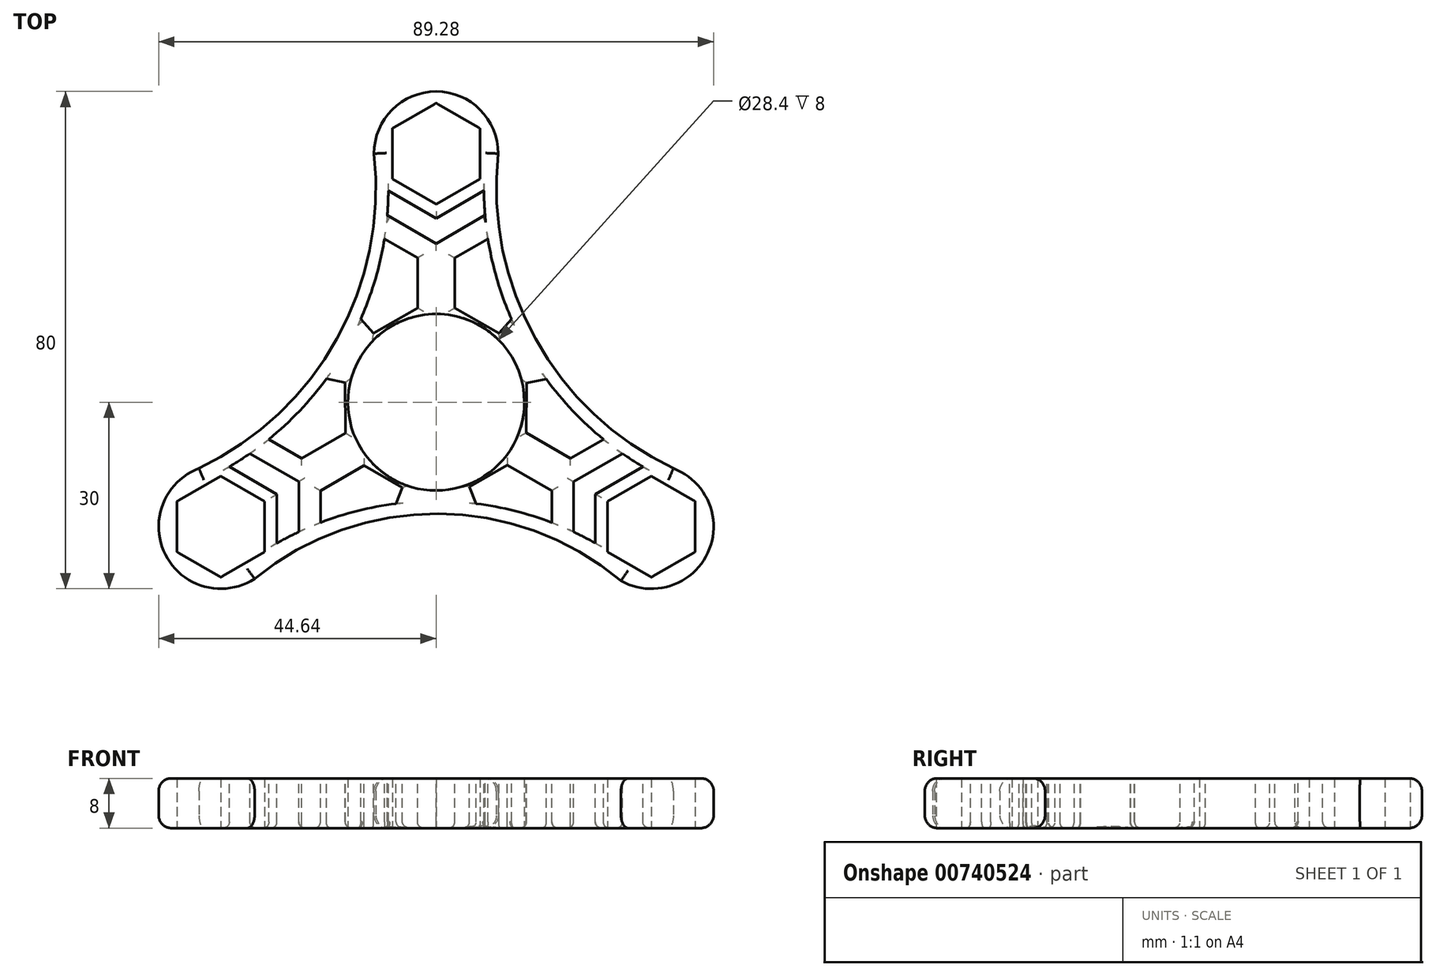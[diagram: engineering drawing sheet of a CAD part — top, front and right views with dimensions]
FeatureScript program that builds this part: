
annotation { "Feature Type Name" : "Feature", "Feature Type Description" : "" }
export const myFeature = defineFeature(function(context is Context, id is Id, definition is map)
    precondition{}
    {
        {
            var Q0;
            Q0=qCreatedBy(makeId("Top.planeOp"),FACE);
            var sketch = newSketch(context, id + "F0", { "sketchPlane" : qUnion([Q0])});
            skPoint(sketch, "E0.0.midPoint", {"position": v(0, 13.42) * mm});
            skLineSegment(sketch, "E1", {"start": v(0, 0) * mm, "end": v(0, 40) * mm});
            skLineSegment(sketch, "E2", {"start": v(0, 0) * mm, "end": v(-34.64, -20) * mm});
            skLineSegment(sketch, "E3", {"start": v(0, 0) * mm, "end": v(34.64, -20) * mm});
            skCircle(sketch, "E4.cCircle", {"center": v(0, 40) * mm, "radius": 7.05 * mm, "construction": true});
            skLineSegment(sketch, "E4.0", {"start": v(-7.05, 35.93) * mm, "end": v(-7.05, 44.07) * mm});
            skLineSegment(sketch, "E4.1", {"start": v(-7.05, 44.07) * mm, "end": v(0, 48.14) * mm});
            skLineSegment(sketch, "E4.2", {"start": v(0, 48.14) * mm, "end": v(7.05, 44.07) * mm});
            skLineSegment(sketch, "E4.3", {"start": v(7.05, 44.07) * mm, "end": v(7.05, 35.93) * mm});
            skLineSegment(sketch, "E4.4", {"start": v(7.05, 35.93) * mm, "end": v(0, 31.86) * mm});
            skLineSegment(sketch, "E4.5", {"start": v(0, 31.86) * mm, "end": v(-7.05, 35.93) * mm});
            skPoint(sketch, "E4.0.midPoint", {"position": v(-7.05, 40) * mm});
            skCircle(sketch, "E5.cCircle", {"center": v(-34.64, -20) * mm, "radius": 7.05 * mm, "construction": true});
            skLineSegment(sketch, "E5.0", {"start": v(-41.7, -24.07) * mm, "end": v(-41.7, -15.93) * mm});
            skLineSegment(sketch, "E5.1", {"start": v(-41.7, -15.93) * mm, "end": v(-34.64, -11.86) * mm});
            skLineSegment(sketch, "E5.2", {"start": v(-34.64, -11.86) * mm, "end": v(-27.6, -15.93) * mm});
            skLineSegment(sketch, "E5.3", {"start": v(-27.6, -15.93) * mm, "end": v(-27.6, -24.07) * mm});
            skLineSegment(sketch, "E5.4", {"start": v(-27.6, -24.07) * mm, "end": v(-34.64, -28.14) * mm});
            skLineSegment(sketch, "E5.5", {"start": v(-34.64, -28.14) * mm, "end": v(-41.7, -24.07) * mm});
            skPoint(sketch, "E5.0.midPoint", {"position": v(-41.7, -20) * mm});
            skCircle(sketch, "E6.cCircle", {"center": v(34.64, -20) * mm, "radius": 7.05 * mm, "construction": true});
            skLineSegment(sketch, "E6.0", {"start": v(41.7, -15.93) * mm, "end": v(41.7, -24.07) * mm});
            skLineSegment(sketch, "E6.1", {"start": v(41.7, -24.07) * mm, "end": v(34.64, -28.14) * mm});
            skLineSegment(sketch, "E6.2", {"start": v(34.64, -28.14) * mm, "end": v(27.6, -24.07) * mm});
            skLineSegment(sketch, "E6.3", {"start": v(27.6, -24.07) * mm, "end": v(27.6, -15.93) * mm});
            skLineSegment(sketch, "E6.4", {"start": v(27.6, -15.93) * mm, "end": v(34.64, -11.86) * mm});
            skLineSegment(sketch, "E6.5", {"start": v(34.64, -11.86) * mm, "end": v(41.7, -15.93) * mm});
            skPoint(sketch, "E6.0.midPoint", {"position": v(41.7, -20) * mm});
            skCircle(sketch, "E7", {"center": v(0, 40) * mm, "radius": 10 * mm});
            skCircle(sketch, "E8", {"center": v(-34.64, -20) * mm, "radius": 10 * mm});
            skCircle(sketch, "E9", {"center": v(34.64, -20) * mm, "radius": 10 * mm});
            skArc(sketch, "E10", {"start": v(-38.17, -10.64) * mm, "mid": v(-16, 10.18) * mm, "end": v(-10, 40) * mm});
            skPoint(sketch, "E10.startSnap0", {"position": v(-38.17, -13.9) * mm});
            skPoint(sketch, "E11.startSnap0", {"position": v(31.12, -26.1) * mm});
            skPoint(sketch, "E11.endSnap0", {"position": v(-31.12, -26.1) * mm});
            skArc(sketch, "E12", {"start": v(10, 40) * mm, "mid": v(16, 10.18) * mm, "end": v(38.17, -10.64) * mm});
            skPoint(sketch, "E12.startSnap0", {"position": v(7.05, 40) * mm});
            skPoint(sketch, "E12.endSnap0", {"position": v(38.17, -13.9) * mm});
            skCircle(sketch, "E13", {"center": v(0, 0) * mm, "radius": 14.2 * mm});
            skArc(sketch, "E14", {"start": v(29.75, -28.72) * mm, "mid": v(0.32, -17.94) * mm, "end": v(-29.22, -28.4) * mm});
            skSolve(sketch);
        }
        {
            var Q0;
            {var subQ0=sQuery(id+"F0.wireOp",EDGE,"E10");var subQ1=sQuery(id+"F0.wireOp",EDGE,"E0.0");var subQ2=makeQuery(id+"F0.imprint","INTERSECT",VERTEX,{"derivedFrom":[subQ1,subQ0]});Q0=makeQuery(id+"F0.imprint","IMPRINT",FACE,{"disambiguationData":[TD([[makeQuery(id+"F0.imprint","IMPRINT",EDGE,{"disambiguationData":[TD([[subQ2,-1.0]])],"derivedFrom":subQ1}),1.0]])]});}
            var Q1;
            Q1=makeQuery(id+"F0.imprint","IMPRINT",FACE,{"disambiguationData":[TD([[makeQuery(id+"F0.imprint","IMPRINT",EDGE,{"derivedFrom":sQuery(id+"F0.wireOp",EDGE,"E4.0")}),1.0]])]});
            var Q2;
            {var subQ0=sQuery(id+"F0.wireOp",EDGE,"E12");var subQ1=sQuery(id+"F0.wireOp",EDGE,"E0.0");var subQ2=makeQuery(id+"F0.imprint","INTERSECT",VERTEX,{"derivedFrom":[subQ1,subQ0]});Q2=makeQuery(id+"F0.imprint","IMPRINT",FACE,{"disambiguationData":[TD([[makeQuery(id+"F0.imprint","IMPRINT",EDGE,{"disambiguationData":[TD([[subQ2,1.0]])],"derivedFrom":subQ1}),1.0]])]});}
            var Q3;
            {var subQ1=sQuery(id+"F0.wireOp",EDGE,"vRD934ja-ZAdI-i6bS-saWl-KqptXDvDajmV");var subQ8=sQuery(id+"F0.wireOp",EDGE,"E2");var subQ11=makeQuery(id+"F0.imprint","INTERSECT",VERTEX,{"derivedFrom":[subQ1,subQ8]});Q3=makeQuery(id+"F0.imprint","IMPRINT",FACE,{"disambiguationData":[TD([[makeQuery(id+"F0.imprint","IMPRINT",EDGE,{"disambiguationData":[TD([[subQ11,1.0]])],"derivedFrom":subQ1}),-1.0]])]});}
            var Q4;
            {var subQ0=sQuery(id+"F0.wireOp",EDGE,"E1");var subQ1=sQuery(id+"F0.wireOp",EDGE,"vRD934ja-ZAdI-i6bS-saWl-KqptXDvDajmV");var subQ2=makeQuery(id+"F0.imprint","INTERSECT",VERTEX,{"derivedFrom":[subQ1,subQ0]});Q4=makeQuery(id+"F0.imprint","IMPRINT",FACE,{"disambiguationData":[TD([[makeQuery(id+"F0.imprint","IMPRINT",EDGE,{"disambiguationData":[TD([[subQ2,1.0]])],"derivedFrom":subQ1}),-1.0]])]});}
            var Q5;
            {var subQ3=sQuery(id+"F0.wireOp",EDGE,"E2");var subQ5=sQuery(id+"F0.wireOp",EDGE,"vRD934ja-ZAdI-i6bS-saWl-KqptXDvDajmV");var subQ6=makeQuery(id+"F0.imprint","INTERSECT",VERTEX,{"derivedFrom":[subQ5,subQ3]});Q5=makeQuery(id+"F0.imprint","IMPRINT",FACE,{"disambiguationData":[TD([[makeQuery(id+"F0.imprint","IMPRINT",EDGE,{"disambiguationData":[TD([[subQ6,-1.0]])],"derivedFrom":subQ5}),-1.0]])]});}
            var Q6;
            {var subQ0=sQuery(id+"F0.wireOp",EDGE,"E11");var subQ1=sQuery(id+"F0.wireOp",EDGE,"E0.2");var subQ2=makeQuery(id+"F0.imprint","INTERSECT",VERTEX,{"derivedFrom":[subQ1,subQ0]});Q6=makeQuery(id+"F0.imprint","IMPRINT",FACE,{"disambiguationData":[TD([[makeQuery(id+"F0.imprint","IMPRINT",EDGE,{"disambiguationData":[TD([[subQ2,-1.0]])],"derivedFrom":subQ1}),1.0]])]});}
            var Q7;
            {var subQ0=sQuery(id+"F0.wireOp",EDGE,"E10");var subQ1=sQuery(id+"F0.wireOp",EDGE,"E0.2");var subQ2=makeQuery(id+"F0.imprint","INTERSECT",VERTEX,{"derivedFrom":[subQ1,subQ0]});Q7=makeQuery(id+"F0.imprint","IMPRINT",FACE,{"disambiguationData":[TD([[makeQuery(id+"F0.imprint","IMPRINT",EDGE,{"disambiguationData":[TD([[subQ2,1.0]])],"derivedFrom":subQ1}),1.0]])]});}
            var Q8;
            Q8=makeQuery(id+"F0.imprint","IMPRINT",FACE,{"disambiguationData":[TD([[makeQuery(id+"F0.imprint","IMPRINT",EDGE,{"derivedFrom":sQuery(id+"F0.wireOp",EDGE,"E5.0")}),1.0]])]});
            var Q9;
            {var subQ0=sQuery(id+"F0.wireOp",EDGE,"E11");var subQ1=sQuery(id+"F0.wireOp",EDGE,"E0.1");var subQ2=makeQuery(id+"F0.imprint","INTERSECT",VERTEX,{"derivedFrom":[subQ1,subQ0]});Q9=makeQuery(id+"F0.imprint","IMPRINT",FACE,{"disambiguationData":[TD([[makeQuery(id+"F0.imprint","IMPRINT",EDGE,{"disambiguationData":[TD([[subQ2,1.0]])],"derivedFrom":subQ1}),1.0]])]});}
            var Q10;
            {var subQ0=sQuery(id+"F0.wireOp",EDGE,"E12");var subQ1=sQuery(id+"F0.wireOp",EDGE,"E0.1");var subQ2=makeQuery(id+"F0.imprint","INTERSECT",VERTEX,{"derivedFrom":[subQ1,subQ0]});Q10=makeQuery(id+"F0.imprint","IMPRINT",FACE,{"disambiguationData":[TD([[makeQuery(id+"F0.imprint","IMPRINT",EDGE,{"disambiguationData":[TD([[subQ2,-1.0]])],"derivedFrom":subQ1}),1.0]])]});}
            var Q11;
            Q11=makeQuery(id+"F0.imprint","IMPRINT",FACE,{"disambiguationData":[TD([[makeQuery(id+"F0.imprint","IMPRINT",EDGE,{"derivedFrom":sQuery(id+"F0.wireOp",EDGE,"E6.0")}),1.0]])]});
            var Q12;
            {var subQ6=sQuery(id+"F0.wireOp",EDGE,"E1");var subQ9=sQuery(id+"F0.wireOp",EDGE,"E7");var subQ10=makeQuery(id+"F0.imprint","INTERSECT",VERTEX,{"derivedFrom":[subQ6,subQ9]});Q12=makeQuery(id+"F0.imprint","IMPRINT",FACE,{"disambiguationData":[TD([[makeQuery(id+"F0.imprint","IMPRINT",EDGE,{"disambiguationData":[TD([[subQ10,1.0]])],"derivedFrom":subQ6}),1.0]])]});}
            var Q13;
            {var subQ5=sQuery(id+"F0.wireOp",EDGE,"E7");var subQ6=sQuery(id+"F0.wireOp",EDGE,"E1");var subQ7=makeQuery(id+"F0.imprint","INTERSECT",VERTEX,{"derivedFrom":[subQ6,subQ5]});Q13=makeQuery(id+"F0.imprint","IMPRINT",FACE,{"disambiguationData":[TD([[makeQuery(id+"F0.imprint","IMPRINT",EDGE,{"disambiguationData":[TD([[subQ7,1.0]])],"derivedFrom":subQ6}),-1.0]])]});}
            var Q14;
            {var subQ0=sQuery(id+"F0.wireOp",EDGE,"LMxYpjUG-xxoM-OBT4-osdf-MFONTkuZMlqp");Q14=makeQuery(id+"F0.imprint","IMPRINT",FACE,{"disambiguationData":[TD([[makeQuery(id+"F0.imprint","IMPRINT",EDGE,{"derivedFrom":subQ0}),-1.0]])]});}
            var Q15;
            {var subQ5=sQuery(id+"F0.wireOp",EDGE,"E8");var subQ7=sQuery(id+"F0.wireOp",EDGE,"E2");var subQ8=makeQuery(id+"F0.imprint","INTERSECT",VERTEX,{"derivedFrom":[subQ7,subQ5]});Q15=makeQuery(id+"F0.imprint","IMPRINT",FACE,{"disambiguationData":[TD([[makeQuery(id+"F0.imprint","IMPRINT",EDGE,{"disambiguationData":[TD([[subQ8,1.0]])],"derivedFrom":subQ7}),1.0]])]});}
            extrude(context, id + "F1", {"entities" : qUnion([Q0, Q1, Q2, Q3, Q4, Q5, Q6, Q7, Q8, Q9, Q10, Q11, Q12, Q13, Q14, Q15]), "depth" : 8 * mm, "offsetDistance" : 25 * mm});
        }
        {
            var Q0;
            Q0=makeQuery(id+"F1.opExtrude","CAP_FACE",FACE,{"disambiguationData":[OSD([sQuery(id+"F0.wireOp",EDGE,"vRD934ja-ZAdI-i6bS-saWl-KqptXDvDajmV"),sQuery(id+"F0.wireOp",EDGE,"E4.0"),sQuery(id+"F0.wireOp",EDGE,"E4.1"),sQuery(id+"F0.wireOp",EDGE,"E4.2"),sQuery(id+"F0.wireOp",EDGE,"E4.3"),sQuery(id+"F0.wireOp",EDGE,"E4.4"),sQuery(id+"F0.wireOp",EDGE,"E4.5"),sQuery(id+"F0.wireOp",EDGE,"E5.0"),sQuery(id+"F0.wireOp",EDGE,"E5.1"),sQuery(id+"F0.wireOp",EDGE,"E5.2"),sQuery(id+"F0.wireOp",EDGE,"E5.3"),sQuery(id+"F0.wireOp",EDGE,"E5.4"),sQuery(id+"F0.wireOp",EDGE,"E5.5"),sQuery(id+"F0.wireOp",EDGE,"E6.0"),sQuery(id+"F0.wireOp",EDGE,"E6.1"),sQuery(id+"F0.wireOp",EDGE,"E6.2"),sQuery(id+"F0.wireOp",EDGE,"E6.3"),sQuery(id+"F0.wireOp",EDGE,"E6.4"),sQuery(id+"F0.wireOp",EDGE,"E6.5"),sQuery(id+"F0.wireOp",EDGE,"E7"),sQuery(id+"F0.wireOp",EDGE,"E8"),sQuery(id+"F0.wireOp",EDGE,"E9"),sQuery(id+"F0.wireOp",EDGE,"E10"),sQuery(id+"F0.wireOp",EDGE,"E12"),sQuery(id+"F0.wireOp",EDGE,"LMxYpjUG-xxoM-OBT4-osdf-MFONTkuZMlqp")])],"isStart":false});
            var sketch = newSketch(context, id + "F2", { "sketchPlane" : qUnion([Q0])});
            skLineSegment(sketch, "E15.0", {"start": v(0, 29.57) * mm, "end": v(-7.7, 34.01) * mm});
            skLineSegment(sketch, "E15.1", {"start": v(7.7, 34.01) * mm, "end": v(0, 29.57) * mm});
            skArc(sketch, "E16.0", {"start": v(36.7, -12.21) * mm, "mid": v(14.1, 9.42) * mm, "end": v(8, 40.1) * mm});
            skArc(sketch, "E16.1", {"start": v(-8, 40.1) * mm, "mid": v(-14.1, 9.42) * mm, "end": v(-36.7, -12.21) * mm});
            skLineSegment(sketch, "E17.0", {"start": v(0, 25.53) * mm, "end": v(-7.87, 30.08) * mm});
            skLineSegment(sketch, "E17.1", {"start": v(7.87, 30.08) * mm, "end": v(0, 25.53) * mm});
            skLineSegment(sketch, "E18.0", {"start": v(-3, 23.22) * mm, "end": v(-8.33, 26.3) * mm});
            skLineSegment(sketch, "E18.1", {"start": v(8.33, 26.3) * mm, "end": v(3, 23.22) * mm});
            skLineSegment(sketch, "E19.0", {"start": v(-14.6, -4.97) * mm, "end": v(-14.63, 3.14) * mm});
            skLineSegment(sketch, "E19.1", {"start": v(3, 15.18) * mm, "end": v(10.09, 11.12) * mm});
            skLineSegment(sketch, "E19.2", {"start": v(14.55, 3.08) * mm, "end": v(14.48, -4.9) * mm});
            skLineSegment(sketch, "E19.3", {"start": v(-10.07, 11.1) * mm, "end": v(-3, 15.17) * mm});
            skLineSegment(sketch, "E19.4", {"start": v(11.45, -10.08) * mm, "end": v(5.37, -13.59) * mm});
            skLineSegment(sketch, "E20.trimOffspring", {"start": v(3, 15.18) * mm, "end": v(3, 23.22) * mm});
            skLineSegment(sketch, "E21.trimOffspring", {"start": v(-3, 15.17) * mm, "end": v(-3, 23.22) * mm});
            skLineSegment(sketch, "E22.0", {"start": v(-25.61, -14.79) * mm, "end": v(-25.61, -22.66) * mm});
            skLineSegment(sketch, "E22.1", {"start": v(-33.27, -10.36) * mm, "end": v(-25.61, -14.79) * mm});
            skLineSegment(sketch, "E23.0", {"start": v(-22.11, -12.77) * mm, "end": v(-22.11, -20.85) * mm});
            skLineSegment(sketch, "E23.1", {"start": v(-29.96, -8.24) * mm, "end": v(-22.11, -12.77) * mm});
            skLineSegment(sketch, "E24.0", {"start": v(-18.61, -10.75) * mm, "end": v(-18.61, -19.36) * mm});
            skLineSegment(sketch, "E24.1", {"start": v(-26.92, -5.95) * mm, "end": v(-18.61, -10.75) * mm});
            skPoint(sketch, "E25.1.start.orphan", {"position": v(0, 0) * mm});
            skArc(sketch, "E26.0", {"start": v(-26.8, -23.36) * mm, "mid": v(0, -15.92) * mm, "end": v(26.8, -23.36) * mm});
            skLineSegment(sketch, "E27.trimOffspring", {"start": v(-11.6, -10.16) * mm, "end": v(-18.61, -14.2) * mm});
            skLineSegment(sketch, "E28.trimOffspring", {"start": v(-14.6, -4.97) * mm, "end": v(-21.61, -9.01) * mm});
            skLineSegment(sketch, "E29.0", {"start": v(25.61, -14.79) * mm, "end": v(33.27, -10.36) * mm});
            skLineSegment(sketch, "E29.1", {"start": v(25.61, -22.66) * mm, "end": v(25.61, -14.79) * mm});
            skLineSegment(sketch, "E30.0", {"start": v(22.11, -12.77) * mm, "end": v(29.96, -8.24) * mm});
            skLineSegment(sketch, "E30.1", {"start": v(22.11, -20.85) * mm, "end": v(22.11, -12.77) * mm});
            skLineSegment(sketch, "E31.0", {"start": v(18.61, -10.75) * mm, "end": v(26.92, -5.95) * mm});
            skLineSegment(sketch, "E31.1", {"start": v(18.61, -19.36) * mm, "end": v(18.61, -10.75) * mm});
            skPoint(sketch, "E32.orphan", {"position": v(-34.64, -20) * mm});
            skPoint(sketch, "E33.trimOffspring.end.orphan", {"position": v(34.64, -20) * mm});
            skLineSegment(sketch, "E34.trimOffspring", {"start": v(14.48, -4.9) * mm, "end": v(21.61, -9.01) * mm});
            skLineSegment(sketch, "E35.trimOffspring", {"start": v(11.45, -10.08) * mm, "end": v(18.61, -14.2) * mm});
            skLineSegment(sketch, "E36", {"start": v(10.09, 11.12) * mm, "end": v(12.14, 13.38) * mm});
            skLineSegment(sketch, "E37", {"start": v(14.55, 3.08) * mm, "end": v(17.7, 3.75) * mm});
            skLineSegment(sketch, "E38", {"start": v(5.37, -13.59) * mm, "end": v(6.45, -16.32) * mm});
            skLineSegment(sketch, "E39", {"start": v(-5.43, -13.72) * mm, "end": v(-6.45, -16.32) * mm});
            skLineSegment(sketch, "E40.trimOffspring", {"start": v(-10.07, 11.1) * mm, "end": v(-12.14, 13.38) * mm});
            skLineSegment(sketch, "E41.trimOffspring", {"start": v(-14.63, 3.14) * mm, "end": v(-17.67, 3.8) * mm});
            skLineSegment(sketch, "E42.trimOffspring", {"start": v(-5.43, -13.72) * mm, "end": v(-11.6, -10.16) * mm});
            skSolve(sketch);
        }
        {
            var Q0;
            {var subQ0=sQuery(id+"F2.wireOp",EDGE,"E15.0");Q0=makeQuery(id+"F2.imprint","IMPRINT",FACE,{"disambiguationData":[TD([[makeQuery(id+"F2.imprint","IMPRINT",EDGE,{"derivedFrom":subQ0}),1.0]])]});}
            var Q1;
            {var subQ0=sQuery(id+"F2.wireOp",EDGE,"E15.1");Q1=makeQuery(id+"F2.imprint","IMPRINT",FACE,{"disambiguationData":[TD([[makeQuery(id+"F2.imprint","IMPRINT",EDGE,{"derivedFrom":subQ0}),1.0]])]});}
            var Q2;
            {var subQ0=sQuery(id+"F2.wireOp",EDGE,"E18.1");Q2=makeQuery(id+"F2.imprint","IMPRINT",FACE,{"disambiguationData":[TD([[makeQuery(id+"F2.imprint","IMPRINT",EDGE,{"derivedFrom":subQ0}),1.0]])]});}
            var Q3;
            Q3=makeQuery(id+"F2.imprint","IMPRINT",FACE,{"disambiguationData":[TD([[makeQuery(id+"F2.imprint","IMPRINT",EDGE,{"derivedFrom":sQuery(id+"F2.wireOp",EDGE,"873998ae-229c-4f65-9336-e61d0cbd62b3.4")}),-1.0]])]});
            var Q4;
            Q4=makeQuery(id+"F2.imprint","IMPRINT",FACE,{"disambiguationData":[TD([[makeQuery(id+"F2.imprint","IMPRINT",EDGE,{"derivedFrom":sQuery(id+"F2.wireOp",EDGE,"873998ae-229c-4f65-9336-e61d0cbd62b3.0")}),-1.0]])]});
            var Q5;
            Q5=makeQuery(id+"F2.imprint","IMPRINT",FACE,{"disambiguationData":[TD([[makeQuery(id+"F2.imprint","IMPRINT",EDGE,{"derivedFrom":sQuery(id+"F2.wireOp",EDGE,"873998ae-229c-4f65-9336-e61d0cbd62b3.3")}),-1.0]])]});
            var Q6;
            {var subQ0=sQuery(id+"F2.wireOp",EDGE,"E19.0");Q6=makeQuery(id+"F2.imprint","IMPRINT",FACE,{"disambiguationData":[TD([[makeQuery(id+"F2.imprint","IMPRINT",EDGE,{"derivedFrom":subQ0}),1.0]])]});}
            var Q7;
            {var subQ0=sQuery(id+"F2.wireOp",EDGE,"E27.trimOffspring");Q7=makeQuery(id+"F2.imprint","IMPRINT",FACE,{"disambiguationData":[TD([[makeQuery(id+"F2.imprint","IMPRINT",EDGE,{"derivedFrom":subQ0}),1.0]])]});}
            var Q8;
            {var subQ1=sQuery(id+"F2.wireOp",EDGE,"E29.0");Q8=makeQuery(id+"F2.imprint","IMPRINT",FACE,{"disambiguationData":[TD([[makeQuery(id+"F2.imprint","IMPRINT",EDGE,{"derivedFrom":subQ1}),1.0]])]});}
            var Q9;
            {var subQ0=sQuery(id+"F2.wireOp",EDGE,"E35.trimOffspring");Q9=makeQuery(id+"F2.imprint","IMPRINT",FACE,{"disambiguationData":[TD([[makeQuery(id+"F2.imprint","IMPRINT",EDGE,{"derivedFrom":subQ0}),-1.0]])]});}
            var Q10;
            {var subQ2=sQuery(id+"F2.wireOp",EDGE,"E22.0");Q10=makeQuery(id+"F2.imprint","IMPRINT",FACE,{"disambiguationData":[TD([[makeQuery(id+"F2.imprint","IMPRINT",EDGE,{"derivedFrom":subQ2}),1.0]])]});}
            var Q11;
            {var subQ0=sQuery(id+"F2.wireOp",EDGE,"E18.0");Q11=makeQuery(id+"F2.imprint","IMPRINT",FACE,{"disambiguationData":[TD([[makeQuery(id+"F2.imprint","IMPRINT",EDGE,{"derivedFrom":subQ0}),1.0]])]});}
            var Q12;
            Q12=makeQuery(id+"F2.imprint","IMPRINT",FACE,{"disambiguationData":[TD([[makeQuery(id+"F2.imprint","IMPRINT",EDGE,{"derivedFrom":sQuery(id+"F2.wireOp",EDGE,"E19.2")}),1.0]])]});
            extrude(context, id + "F3", {"entities" : qUnion([Q0, Q1, Q2, Q3, Q4, Q5, Q6, Q7, Q8, Q9, Q10, Q11, Q12]), "operationType" : NewBodyOperationType.REMOVE, "oppositeDirection" : true, "depth" : 10 * mm, "offsetDistance" : 25 * mm});
        }
        {
            var Q0;
            Q0=makeQuery(id+"F1.opExtrude","CAP_EDGE",EDGE,{"disambiguationData":[OSD([sQuery(id+"F0.wireOp",EDGE,"E10")])],"isStart":false});
            var Q1;
            Q1=makeQuery(id+"F1.opExtrude","CAP_EDGE",EDGE,{"disambiguationData":[OSD([sQuery(id+"F0.wireOp",EDGE,"E8")])],"isStart":false});
            var Q2;
            Q2=makeQuery(id+"F1.opExtrude","CAP_EDGE",EDGE,{"disambiguationData":[OSD([sQuery(id+"F0.wireOp",EDGE,"E14")])],"isStart":false});
            var Q3;
            Q3=makeQuery(id+"F1.opExtrude","CAP_EDGE",EDGE,{"disambiguationData":[OSD([sQuery(id+"F0.wireOp",EDGE,"E9")])],"isStart":false});
            var Q4;
            Q4=makeQuery(id+"F1.opExtrude","CAP_EDGE",EDGE,{"disambiguationData":[OSD([sQuery(id+"F0.wireOp",EDGE,"E12")])],"isStart":false});
            var Q5;
            Q5=makeQuery(id+"F1.opExtrude","CAP_EDGE",EDGE,{"disambiguationData":[OSD([sQuery(id+"F0.wireOp",EDGE,"E7")])],"isStart":false});
            var Q6;
            Q6=makeQuery(id+"F1.opExtrude","CAP_EDGE",EDGE,{"disambiguationData":[OSD([sQuery(id+"F0.wireOp",EDGE,"E10")])],"isStart":true});
            var Q7;
            Q7=makeQuery(id+"F1.opExtrude","CAP_EDGE",EDGE,{"disambiguationData":[OSD([sQuery(id+"F0.wireOp",EDGE,"E7")])],"isStart":true});
            var Q8;
            Q8=makeQuery(id+"F1.opExtrude","CAP_EDGE",EDGE,{"disambiguationData":[OSD([sQuery(id+"F0.wireOp",EDGE,"E12")])],"isStart":true});
            var Q9;
            Q9=makeQuery(id+"F1.opExtrude","CAP_EDGE",EDGE,{"disambiguationData":[OSD([sQuery(id+"F0.wireOp",EDGE,"E9")])],"isStart":true});
            var Q10;
            Q10=makeQuery(id+"F1.opExtrude","CAP_EDGE",EDGE,{"disambiguationData":[OSD([sQuery(id+"F0.wireOp",EDGE,"E14")])],"isStart":true});
            var Q11;
            Q11=makeQuery(id+"F1.opExtrude","CAP_EDGE",EDGE,{"disambiguationData":[OSD([sQuery(id+"F0.wireOp",EDGE,"E8")])],"isStart":true});
            fillet(context, id + "F4", {"entities" : qUnion([Q0, Q1, Q2, Q3, Q4, Q5, Q6, Q7, Q8, Q9, Q10, Q11]), "radius" : 2.03 * mm, "tangentPropagation" : true, "allowEdgeOverflow" : false});
        }
        {
            var Q0;
            Q0=makeQuery(id+"F3.boolean.opBoolean","COPY",EDGE,{"derivedFrom":makeQuery(id+"F3.opExtrude","CAP_EDGE",EDGE,{"disambiguationData":[OSD([sQuery(id+"F2.wireOp",EDGE,"E29.0")])],"isStart":true})});
            var Q1;
            Q1=makeQuery(id+"F3.boolean.opBoolean","COPY",EDGE,{"derivedFrom":makeQuery(id+"F3.opExtrude","CAP_EDGE",EDGE,{"disambiguationData":[OSD([sQuery(id+"F2.wireOp",EDGE,"E29.1")])],"isStart":true})});
            var Q2;
            Q2=makeQuery(id+"F3.boolean.opBoolean","COPY",EDGE,{"derivedFrom":makeQuery(id+"F3.opExtrude","CAP_EDGE",EDGE,{"disambiguationData":[OSD([sQuery(id+"F2.wireOp",EDGE,"E30.0")])],"isStart":true})});
            var Q3;
            Q3=makeQuery(id+"F3.boolean.opBoolean","COPY",EDGE,{"derivedFrom":makeQuery(id+"F3.opExtrude","CAP_EDGE",EDGE,{"disambiguationData":[OSD([sQuery(id+"F2.wireOp",EDGE,"E30.1")])],"isStart":true})});
            var Q4;
            Q4=makeQuery(id+"F3.boolean.opBoolean","COPY",EDGE,{"derivedFrom":makeQuery(id+"F3.opExtrude","CAP_EDGE",EDGE,{"disambiguationData":[OSD([sQuery(id+"F2.wireOp",EDGE,"E31.1")])],"isStart":true})});
            var Q5;
            Q5=makeQuery(id+"F3.boolean.opBoolean","COPY",EDGE,{"derivedFrom":makeQuery(id+"F3.opExtrude","CAP_EDGE",EDGE,{"disambiguationData":[OSD([sQuery(id+"F2.wireOp",EDGE,"E35.trimOffspring")])],"isStart":true})});
            var Q6;
            Q6=makeQuery(id+"F3.boolean.opBoolean","COPY",EDGE,{"derivedFrom":makeQuery(id+"F3.opExtrude","CAP_EDGE",EDGE,{"disambiguationData":[OSD([sQuery(id+"F2.wireOp",EDGE,"E34.trimOffspring")])],"isStart":true})});
            var Q7;
            Q7=makeQuery(id+"F3.boolean.opBoolean","COPY",EDGE,{"derivedFrom":makeQuery(id+"F3.opExtrude","CAP_EDGE",EDGE,{"disambiguationData":[OSD([sQuery(id+"F2.wireOp",EDGE,"E31.0")])],"isStart":true})});
            var Q8;
            Q8=makeQuery(id+"F3.boolean.opBoolean","COPY",EDGE,{"derivedFrom":makeQuery(id+"F3.opExtrude","CAP_EDGE",EDGE,{"disambiguationData":[OSD([sQuery(id+"F2.wireOp",EDGE,"E19.4")])],"isStart":true})});
            var Q9;
            Q9=makeQuery(id+"F3.boolean.opBoolean","COPY",EDGE,{"derivedFrom":makeQuery(id+"F3.opExtrude","CAP_EDGE",EDGE,{"disambiguationData":[OSD([sQuery(id+"F2.wireOp",EDGE,"E38")])],"isStart":true})});
            var Q10;
            Q10=makeQuery(id+"F3.boolean.opBoolean","COPY",EDGE,{"derivedFrom":makeQuery(id+"F3.opExtrude","CAP_EDGE",EDGE,{"disambiguationData":[OSD([sQuery(id+"F2.wireOp",EDGE,"E19.2")])],"isStart":true})});
            var Q11;
            Q11=makeQuery(id+"F3.boolean.opBoolean","COPY",EDGE,{"derivedFrom":makeQuery(id+"F3.opExtrude","CAP_EDGE",EDGE,{"disambiguationData":[OSD([sQuery(id+"F2.wireOp",EDGE,"E37")])],"isStart":true})});
            var Q12;
            Q12=makeQuery(id+"F3.boolean.opBoolean","COPY",EDGE,{"derivedFrom":makeQuery(id+"F3.opExtrude","CAP_EDGE",EDGE,{"disambiguationData":[OSD([sQuery(id+"F2.wireOp",EDGE,"E39")])],"isStart":true})});
            var Q13;
            Q13=makeQuery(id+"F3.boolean.opBoolean","COPY",EDGE,{"derivedFrom":makeQuery(id+"F3.opExtrude","CAP_EDGE",EDGE,{"disambiguationData":[OSD([sQuery(id+"F2.wireOp",EDGE,"E42.trimOffspring")])],"isStart":true})});
            var Q14;
            Q14=makeQuery(id+"F3.boolean.opBoolean","COPY",EDGE,{"derivedFrom":makeQuery(id+"F3.opExtrude","CAP_EDGE",EDGE,{"disambiguationData":[OSD([sQuery(id+"F2.wireOp",EDGE,"E27.trimOffspring")])],"isStart":true})});
            var Q15;
            Q15=makeQuery(id+"F3.boolean.opBoolean","COPY",EDGE,{"derivedFrom":makeQuery(id+"F3.opExtrude","CAP_EDGE",EDGE,{"disambiguationData":[OSD([sQuery(id+"F2.wireOp",EDGE,"E24.0")])],"isStart":true})});
            var Q16;
            Q16=makeQuery(id+"F3.boolean.opBoolean","COPY",EDGE,{"derivedFrom":makeQuery(id+"F3.opExtrude","CAP_EDGE",EDGE,{"disambiguationData":[OSD([sQuery(id+"F2.wireOp",EDGE,"E23.0")])],"isStart":true})});
            var Q17;
            Q17=makeQuery(id+"F3.boolean.opBoolean","COPY",EDGE,{"derivedFrom":makeQuery(id+"F3.opExtrude","CAP_EDGE",EDGE,{"disambiguationData":[OSD([sQuery(id+"F2.wireOp",EDGE,"E22.0")])],"isStart":true})});
            var Q18;
            Q18=makeQuery(id+"F3.boolean.opBoolean","COPY",EDGE,{"derivedFrom":makeQuery(id+"F3.opExtrude","CAP_EDGE",EDGE,{"disambiguationData":[OSD([sQuery(id+"F2.wireOp",EDGE,"E23.1")])],"isStart":true})});
            var Q19;
            Q19=makeQuery(id+"F3.boolean.opBoolean","COPY",EDGE,{"derivedFrom":makeQuery(id+"F3.opExtrude","CAP_EDGE",EDGE,{"disambiguationData":[OSD([sQuery(id+"F2.wireOp",EDGE,"E22.1")])],"isStart":true})});
            var Q20;
            Q20=makeQuery(id+"F3.boolean.opBoolean","COPY",EDGE,{"derivedFrom":makeQuery(id+"F3.opExtrude","CAP_EDGE",EDGE,{"disambiguationData":[OSD([sQuery(id+"F2.wireOp",EDGE,"E24.1")])],"isStart":true})});
            var Q21;
            Q21=makeQuery(id+"F3.boolean.opBoolean","COPY",EDGE,{"derivedFrom":makeQuery(id+"F3.opExtrude","CAP_EDGE",EDGE,{"disambiguationData":[OSD([sQuery(id+"F2.wireOp",EDGE,"E28.trimOffspring")])],"isStart":true})});
            var Q22;
            Q22=makeQuery(id+"F3.boolean.opBoolean","COPY",EDGE,{"derivedFrom":makeQuery(id+"F3.opExtrude","CAP_EDGE",EDGE,{"disambiguationData":[OSD([sQuery(id+"F2.wireOp",EDGE,"E19.0")])],"isStart":true})});
            var Q23;
            Q23=makeQuery(id+"F3.boolean.opBoolean","COPY",EDGE,{"derivedFrom":makeQuery(id+"F3.opExtrude","CAP_EDGE",EDGE,{"disambiguationData":[OSD([sQuery(id+"F2.wireOp",EDGE,"E41.trimOffspring")])],"isStart":true})});
            var Q24;
            Q24=makeQuery(id+"F3.boolean.opBoolean","COPY",EDGE,{"derivedFrom":makeQuery(id+"F3.opExtrude","CAP_EDGE",EDGE,{"disambiguationData":[OSD([sQuery(id+"F2.wireOp",EDGE,"E36")])],"isStart":true})});
            var Q25;
            Q25=makeQuery(id+"F3.boolean.opBoolean","COPY",EDGE,{"derivedFrom":makeQuery(id+"F3.opExtrude","CAP_EDGE",EDGE,{"disambiguationData":[OSD([sQuery(id+"F2.wireOp",EDGE,"E19.1")])],"isStart":true})});
            var Q26;
            Q26=makeQuery(id+"F3.boolean.opBoolean","COPY",EDGE,{"derivedFrom":makeQuery(id+"F3.opExtrude","CAP_EDGE",EDGE,{"disambiguationData":[OSD([sQuery(id+"F2.wireOp",EDGE,"E20.trimOffspring")])],"isStart":true})});
            var Q27;
            Q27=makeQuery(id+"F3.boolean.opBoolean","COPY",EDGE,{"derivedFrom":makeQuery(id+"F3.opExtrude","CAP_EDGE",EDGE,{"disambiguationData":[OSD([sQuery(id+"F2.wireOp",EDGE,"E18.1")])],"isStart":true})});
            var Q28;
            Q28=makeQuery(id+"F3.boolean.opBoolean","COPY",EDGE,{"derivedFrom":makeQuery(id+"F3.opExtrude","CAP_EDGE",EDGE,{"disambiguationData":[OSD([sQuery(id+"F2.wireOp",EDGE,"E21.trimOffspring")])],"isStart":true})});
            var Q29;
            Q29=makeQuery(id+"F3.boolean.opBoolean","COPY",EDGE,{"derivedFrom":makeQuery(id+"F3.opExtrude","CAP_EDGE",EDGE,{"disambiguationData":[OSD([sQuery(id+"F2.wireOp",EDGE,"E18.0")])],"isStart":true})});
            var Q30;
            Q30=makeQuery(id+"F3.boolean.opBoolean","COPY",EDGE,{"derivedFrom":makeQuery(id+"F3.opExtrude","CAP_EDGE",EDGE,{"disambiguationData":[OSD([sQuery(id+"F2.wireOp",EDGE,"E17.0")])],"isStart":true})});
            var Q31;
            Q31=makeQuery(id+"F3.boolean.opBoolean","COPY",EDGE,{"derivedFrom":makeQuery(id+"F3.opExtrude","CAP_EDGE",EDGE,{"disambiguationData":[OSD([sQuery(id+"F2.wireOp",EDGE,"E17.1")])],"isStart":true})});
            var Q32;
            Q32=makeQuery(id+"F3.boolean.opBoolean","COPY",EDGE,{"derivedFrom":makeQuery(id+"F3.opExtrude","CAP_EDGE",EDGE,{"disambiguationData":[OSD([sQuery(id+"F2.wireOp",EDGE,"E15.1")])],"isStart":true})});
            var Q33;
            Q33=makeQuery(id+"F3.boolean.opBoolean","COPY",EDGE,{"derivedFrom":makeQuery(id+"F3.opExtrude","CAP_EDGE",EDGE,{"disambiguationData":[OSD([sQuery(id+"F2.wireOp",EDGE,"E15.0")])],"isStart":true})});
            var Q34;
            Q34=makeQuery(id+"F3.boolean.opBoolean","INTERSECT",EDGE,{"derivedFrom":[makeQuery(id+"F1.opExtrude","CAP_FACE",FACE,{"disambiguationData":[OSD([sQuery(id+"F0.wireOp",EDGE,"E4.0"),sQuery(id+"F0.wireOp",EDGE,"E4.1"),sQuery(id+"F0.wireOp",EDGE,"E4.2"),sQuery(id+"F0.wireOp",EDGE,"E4.3"),sQuery(id+"F0.wireOp",EDGE,"E4.4"),sQuery(id+"F0.wireOp",EDGE,"E4.5"),sQuery(id+"F0.wireOp",EDGE,"E5.0"),sQuery(id+"F0.wireOp",EDGE,"E5.1"),sQuery(id+"F0.wireOp",EDGE,"E5.2"),sQuery(id+"F0.wireOp",EDGE,"E5.3"),sQuery(id+"F0.wireOp",EDGE,"E5.4"),sQuery(id+"F0.wireOp",EDGE,"E5.5"),sQuery(id+"F0.wireOp",EDGE,"E6.0"),sQuery(id+"F0.wireOp",EDGE,"E6.1"),sQuery(id+"F0.wireOp",EDGE,"E6.2"),sQuery(id+"F0.wireOp",EDGE,"E6.3"),sQuery(id+"F0.wireOp",EDGE,"E6.4"),sQuery(id+"F0.wireOp",EDGE,"E6.5"),sQuery(id+"F0.wireOp",EDGE,"E7"),sQuery(id+"F0.wireOp",EDGE,"E8"),sQuery(id+"F0.wireOp",EDGE,"E9"),sQuery(id+"F0.wireOp",EDGE,"E10"),sQuery(id+"F0.wireOp",EDGE,"E12"),sQuery(id+"F0.wireOp",EDGE,"E13"),sQuery(id+"F0.wireOp",EDGE,"E14")])],"isStart":true}),makeQuery(id+"F3.opExtrude","SWEPT_FACE",FACE,{"disambiguationData":[OSD([sQuery(id+"F2.wireOp",EDGE,"E29.1")])]})]});
            var Q35;
            Q35=makeQuery(id+"F3.boolean.opBoolean","INTERSECT",EDGE,{"derivedFrom":[makeQuery(id+"F1.opExtrude","CAP_FACE",FACE,{"disambiguationData":[OSD([sQuery(id+"F0.wireOp",EDGE,"E4.0"),sQuery(id+"F0.wireOp",EDGE,"E4.1"),sQuery(id+"F0.wireOp",EDGE,"E4.2"),sQuery(id+"F0.wireOp",EDGE,"E4.3"),sQuery(id+"F0.wireOp",EDGE,"E4.4"),sQuery(id+"F0.wireOp",EDGE,"E4.5"),sQuery(id+"F0.wireOp",EDGE,"E5.0"),sQuery(id+"F0.wireOp",EDGE,"E5.1"),sQuery(id+"F0.wireOp",EDGE,"E5.2"),sQuery(id+"F0.wireOp",EDGE,"E5.3"),sQuery(id+"F0.wireOp",EDGE,"E5.4"),sQuery(id+"F0.wireOp",EDGE,"E5.5"),sQuery(id+"F0.wireOp",EDGE,"E6.0"),sQuery(id+"F0.wireOp",EDGE,"E6.1"),sQuery(id+"F0.wireOp",EDGE,"E6.2"),sQuery(id+"F0.wireOp",EDGE,"E6.3"),sQuery(id+"F0.wireOp",EDGE,"E6.4"),sQuery(id+"F0.wireOp",EDGE,"E6.5"),sQuery(id+"F0.wireOp",EDGE,"E7"),sQuery(id+"F0.wireOp",EDGE,"E8"),sQuery(id+"F0.wireOp",EDGE,"E9"),sQuery(id+"F0.wireOp",EDGE,"E10"),sQuery(id+"F0.wireOp",EDGE,"E12"),sQuery(id+"F0.wireOp",EDGE,"E13"),sQuery(id+"F0.wireOp",EDGE,"E14")])],"isStart":true}),makeQuery(id+"F3.opExtrude","SWEPT_FACE",FACE,{"disambiguationData":[OSD([sQuery(id+"F2.wireOp",EDGE,"E29.0")])]})]});
            var Q36;
            Q36=makeQuery(id+"F3.boolean.opBoolean","INTERSECT",EDGE,{"derivedFrom":[makeQuery(id+"F1.opExtrude","CAP_FACE",FACE,{"disambiguationData":[OSD([sQuery(id+"F0.wireOp",EDGE,"E4.0"),sQuery(id+"F0.wireOp",EDGE,"E4.1"),sQuery(id+"F0.wireOp",EDGE,"E4.2"),sQuery(id+"F0.wireOp",EDGE,"E4.3"),sQuery(id+"F0.wireOp",EDGE,"E4.4"),sQuery(id+"F0.wireOp",EDGE,"E4.5"),sQuery(id+"F0.wireOp",EDGE,"E5.0"),sQuery(id+"F0.wireOp",EDGE,"E5.1"),sQuery(id+"F0.wireOp",EDGE,"E5.2"),sQuery(id+"F0.wireOp",EDGE,"E5.3"),sQuery(id+"F0.wireOp",EDGE,"E5.4"),sQuery(id+"F0.wireOp",EDGE,"E5.5"),sQuery(id+"F0.wireOp",EDGE,"E6.0"),sQuery(id+"F0.wireOp",EDGE,"E6.1"),sQuery(id+"F0.wireOp",EDGE,"E6.2"),sQuery(id+"F0.wireOp",EDGE,"E6.3"),sQuery(id+"F0.wireOp",EDGE,"E6.4"),sQuery(id+"F0.wireOp",EDGE,"E6.5"),sQuery(id+"F0.wireOp",EDGE,"E7"),sQuery(id+"F0.wireOp",EDGE,"E8"),sQuery(id+"F0.wireOp",EDGE,"E9"),sQuery(id+"F0.wireOp",EDGE,"E10"),sQuery(id+"F0.wireOp",EDGE,"E12"),sQuery(id+"F0.wireOp",EDGE,"E13"),sQuery(id+"F0.wireOp",EDGE,"E14")])],"isStart":true}),makeQuery(id+"F3.opExtrude","SWEPT_FACE",FACE,{"disambiguationData":[OSD([sQuery(id+"F2.wireOp",EDGE,"E30.0")])]})]});
            var Q37;
            Q37=makeQuery(id+"F3.boolean.opBoolean","INTERSECT",EDGE,{"derivedFrom":[makeQuery(id+"F1.opExtrude","CAP_FACE",FACE,{"disambiguationData":[OSD([sQuery(id+"F0.wireOp",EDGE,"E4.0"),sQuery(id+"F0.wireOp",EDGE,"E4.1"),sQuery(id+"F0.wireOp",EDGE,"E4.2"),sQuery(id+"F0.wireOp",EDGE,"E4.3"),sQuery(id+"F0.wireOp",EDGE,"E4.4"),sQuery(id+"F0.wireOp",EDGE,"E4.5"),sQuery(id+"F0.wireOp",EDGE,"E5.0"),sQuery(id+"F0.wireOp",EDGE,"E5.1"),sQuery(id+"F0.wireOp",EDGE,"E5.2"),sQuery(id+"F0.wireOp",EDGE,"E5.3"),sQuery(id+"F0.wireOp",EDGE,"E5.4"),sQuery(id+"F0.wireOp",EDGE,"E5.5"),sQuery(id+"F0.wireOp",EDGE,"E6.0"),sQuery(id+"F0.wireOp",EDGE,"E6.1"),sQuery(id+"F0.wireOp",EDGE,"E6.2"),sQuery(id+"F0.wireOp",EDGE,"E6.3"),sQuery(id+"F0.wireOp",EDGE,"E6.4"),sQuery(id+"F0.wireOp",EDGE,"E6.5"),sQuery(id+"F0.wireOp",EDGE,"E7"),sQuery(id+"F0.wireOp",EDGE,"E8"),sQuery(id+"F0.wireOp",EDGE,"E9"),sQuery(id+"F0.wireOp",EDGE,"E10"),sQuery(id+"F0.wireOp",EDGE,"E12"),sQuery(id+"F0.wireOp",EDGE,"E13"),sQuery(id+"F0.wireOp",EDGE,"E14")])],"isStart":true}),makeQuery(id+"F3.opExtrude","SWEPT_FACE",FACE,{"disambiguationData":[OSD([sQuery(id+"F2.wireOp",EDGE,"E30.1")])]})]});
            var Q38;
            Q38=makeQuery(id+"F3.boolean.opBoolean","INTERSECT",EDGE,{"derivedFrom":[makeQuery(id+"F1.opExtrude","CAP_FACE",FACE,{"disambiguationData":[OSD([sQuery(id+"F0.wireOp",EDGE,"E4.0"),sQuery(id+"F0.wireOp",EDGE,"E4.1"),sQuery(id+"F0.wireOp",EDGE,"E4.2"),sQuery(id+"F0.wireOp",EDGE,"E4.3"),sQuery(id+"F0.wireOp",EDGE,"E4.4"),sQuery(id+"F0.wireOp",EDGE,"E4.5"),sQuery(id+"F0.wireOp",EDGE,"E5.0"),sQuery(id+"F0.wireOp",EDGE,"E5.1"),sQuery(id+"F0.wireOp",EDGE,"E5.2"),sQuery(id+"F0.wireOp",EDGE,"E5.3"),sQuery(id+"F0.wireOp",EDGE,"E5.4"),sQuery(id+"F0.wireOp",EDGE,"E5.5"),sQuery(id+"F0.wireOp",EDGE,"E6.0"),sQuery(id+"F0.wireOp",EDGE,"E6.1"),sQuery(id+"F0.wireOp",EDGE,"E6.2"),sQuery(id+"F0.wireOp",EDGE,"E6.3"),sQuery(id+"F0.wireOp",EDGE,"E6.4"),sQuery(id+"F0.wireOp",EDGE,"E6.5"),sQuery(id+"F0.wireOp",EDGE,"E7"),sQuery(id+"F0.wireOp",EDGE,"E8"),sQuery(id+"F0.wireOp",EDGE,"E9"),sQuery(id+"F0.wireOp",EDGE,"E10"),sQuery(id+"F0.wireOp",EDGE,"E12"),sQuery(id+"F0.wireOp",EDGE,"E13"),sQuery(id+"F0.wireOp",EDGE,"E14")])],"isStart":true}),makeQuery(id+"F3.opExtrude","SWEPT_FACE",FACE,{"disambiguationData":[OSD([sQuery(id+"F2.wireOp",EDGE,"E35.trimOffspring")])]})]});
            var Q39;
            Q39=makeQuery(id+"F3.boolean.opBoolean","INTERSECT",EDGE,{"derivedFrom":[makeQuery(id+"F1.opExtrude","CAP_FACE",FACE,{"disambiguationData":[OSD([sQuery(id+"F0.wireOp",EDGE,"E4.0"),sQuery(id+"F0.wireOp",EDGE,"E4.1"),sQuery(id+"F0.wireOp",EDGE,"E4.2"),sQuery(id+"F0.wireOp",EDGE,"E4.3"),sQuery(id+"F0.wireOp",EDGE,"E4.4"),sQuery(id+"F0.wireOp",EDGE,"E4.5"),sQuery(id+"F0.wireOp",EDGE,"E5.0"),sQuery(id+"F0.wireOp",EDGE,"E5.1"),sQuery(id+"F0.wireOp",EDGE,"E5.2"),sQuery(id+"F0.wireOp",EDGE,"E5.3"),sQuery(id+"F0.wireOp",EDGE,"E5.4"),sQuery(id+"F0.wireOp",EDGE,"E5.5"),sQuery(id+"F0.wireOp",EDGE,"E6.0"),sQuery(id+"F0.wireOp",EDGE,"E6.1"),sQuery(id+"F0.wireOp",EDGE,"E6.2"),sQuery(id+"F0.wireOp",EDGE,"E6.3"),sQuery(id+"F0.wireOp",EDGE,"E6.4"),sQuery(id+"F0.wireOp",EDGE,"E6.5"),sQuery(id+"F0.wireOp",EDGE,"E7"),sQuery(id+"F0.wireOp",EDGE,"E8"),sQuery(id+"F0.wireOp",EDGE,"E9"),sQuery(id+"F0.wireOp",EDGE,"E10"),sQuery(id+"F0.wireOp",EDGE,"E12"),sQuery(id+"F0.wireOp",EDGE,"E13"),sQuery(id+"F0.wireOp",EDGE,"E14")])],"isStart":true}),makeQuery(id+"F3.opExtrude","SWEPT_FACE",FACE,{"disambiguationData":[OSD([sQuery(id+"F2.wireOp",EDGE,"E19.4")])]})]});
            var Q40;
            Q40=makeQuery(id+"F3.boolean.opBoolean","INTERSECT",EDGE,{"derivedFrom":[makeQuery(id+"F1.opExtrude","CAP_FACE",FACE,{"disambiguationData":[OSD([sQuery(id+"F0.wireOp",EDGE,"E4.0"),sQuery(id+"F0.wireOp",EDGE,"E4.1"),sQuery(id+"F0.wireOp",EDGE,"E4.2"),sQuery(id+"F0.wireOp",EDGE,"E4.3"),sQuery(id+"F0.wireOp",EDGE,"E4.4"),sQuery(id+"F0.wireOp",EDGE,"E4.5"),sQuery(id+"F0.wireOp",EDGE,"E5.0"),sQuery(id+"F0.wireOp",EDGE,"E5.1"),sQuery(id+"F0.wireOp",EDGE,"E5.2"),sQuery(id+"F0.wireOp",EDGE,"E5.3"),sQuery(id+"F0.wireOp",EDGE,"E5.4"),sQuery(id+"F0.wireOp",EDGE,"E5.5"),sQuery(id+"F0.wireOp",EDGE,"E6.0"),sQuery(id+"F0.wireOp",EDGE,"E6.1"),sQuery(id+"F0.wireOp",EDGE,"E6.2"),sQuery(id+"F0.wireOp",EDGE,"E6.3"),sQuery(id+"F0.wireOp",EDGE,"E6.4"),sQuery(id+"F0.wireOp",EDGE,"E6.5"),sQuery(id+"F0.wireOp",EDGE,"E7"),sQuery(id+"F0.wireOp",EDGE,"E8"),sQuery(id+"F0.wireOp",EDGE,"E9"),sQuery(id+"F0.wireOp",EDGE,"E10"),sQuery(id+"F0.wireOp",EDGE,"E12"),sQuery(id+"F0.wireOp",EDGE,"E13"),sQuery(id+"F0.wireOp",EDGE,"E14")])],"isStart":true}),makeQuery(id+"F3.opExtrude","SWEPT_FACE",FACE,{"disambiguationData":[OSD([sQuery(id+"F2.wireOp",EDGE,"E31.1")])]})]});
            var Q41;
            Q41=makeQuery(id+"F3.boolean.opBoolean","INTERSECT",EDGE,{"derivedFrom":[makeQuery(id+"F1.opExtrude","CAP_FACE",FACE,{"disambiguationData":[OSD([sQuery(id+"F0.wireOp",EDGE,"E4.0"),sQuery(id+"F0.wireOp",EDGE,"E4.1"),sQuery(id+"F0.wireOp",EDGE,"E4.2"),sQuery(id+"F0.wireOp",EDGE,"E4.3"),sQuery(id+"F0.wireOp",EDGE,"E4.4"),sQuery(id+"F0.wireOp",EDGE,"E4.5"),sQuery(id+"F0.wireOp",EDGE,"E5.0"),sQuery(id+"F0.wireOp",EDGE,"E5.1"),sQuery(id+"F0.wireOp",EDGE,"E5.2"),sQuery(id+"F0.wireOp",EDGE,"E5.3"),sQuery(id+"F0.wireOp",EDGE,"E5.4"),sQuery(id+"F0.wireOp",EDGE,"E5.5"),sQuery(id+"F0.wireOp",EDGE,"E6.0"),sQuery(id+"F0.wireOp",EDGE,"E6.1"),sQuery(id+"F0.wireOp",EDGE,"E6.2"),sQuery(id+"F0.wireOp",EDGE,"E6.3"),sQuery(id+"F0.wireOp",EDGE,"E6.4"),sQuery(id+"F0.wireOp",EDGE,"E6.5"),sQuery(id+"F0.wireOp",EDGE,"E7"),sQuery(id+"F0.wireOp",EDGE,"E8"),sQuery(id+"F0.wireOp",EDGE,"E9"),sQuery(id+"F0.wireOp",EDGE,"E10"),sQuery(id+"F0.wireOp",EDGE,"E12"),sQuery(id+"F0.wireOp",EDGE,"E13"),sQuery(id+"F0.wireOp",EDGE,"E14")])],"isStart":true}),makeQuery(id+"F3.opExtrude","SWEPT_FACE",FACE,{"disambiguationData":[OSD([sQuery(id+"F2.wireOp",EDGE,"E38")])]})]});
            var Q42;
            Q42=makeQuery(id+"F3.boolean.opBoolean","INTERSECT",EDGE,{"derivedFrom":[makeQuery(id+"F1.opExtrude","CAP_FACE",FACE,{"disambiguationData":[OSD([sQuery(id+"F0.wireOp",EDGE,"E4.0"),sQuery(id+"F0.wireOp",EDGE,"E4.1"),sQuery(id+"F0.wireOp",EDGE,"E4.2"),sQuery(id+"F0.wireOp",EDGE,"E4.3"),sQuery(id+"F0.wireOp",EDGE,"E4.4"),sQuery(id+"F0.wireOp",EDGE,"E4.5"),sQuery(id+"F0.wireOp",EDGE,"E5.0"),sQuery(id+"F0.wireOp",EDGE,"E5.1"),sQuery(id+"F0.wireOp",EDGE,"E5.2"),sQuery(id+"F0.wireOp",EDGE,"E5.3"),sQuery(id+"F0.wireOp",EDGE,"E5.4"),sQuery(id+"F0.wireOp",EDGE,"E5.5"),sQuery(id+"F0.wireOp",EDGE,"E6.0"),sQuery(id+"F0.wireOp",EDGE,"E6.1"),sQuery(id+"F0.wireOp",EDGE,"E6.2"),sQuery(id+"F0.wireOp",EDGE,"E6.3"),sQuery(id+"F0.wireOp",EDGE,"E6.4"),sQuery(id+"F0.wireOp",EDGE,"E6.5"),sQuery(id+"F0.wireOp",EDGE,"E7"),sQuery(id+"F0.wireOp",EDGE,"E8"),sQuery(id+"F0.wireOp",EDGE,"E9"),sQuery(id+"F0.wireOp",EDGE,"E10"),sQuery(id+"F0.wireOp",EDGE,"E12"),sQuery(id+"F0.wireOp",EDGE,"E13"),sQuery(id+"F0.wireOp",EDGE,"E14")])],"isStart":true}),makeQuery(id+"F3.opExtrude","SWEPT_FACE",FACE,{"disambiguationData":[OSD([sQuery(id+"F2.wireOp",EDGE,"E34.trimOffspring")])]})]});
            var Q43;
            Q43=makeQuery(id+"F3.boolean.opBoolean","INTERSECT",EDGE,{"derivedFrom":[makeQuery(id+"F1.opExtrude","CAP_FACE",FACE,{"disambiguationData":[OSD([sQuery(id+"F0.wireOp",EDGE,"E4.0"),sQuery(id+"F0.wireOp",EDGE,"E4.1"),sQuery(id+"F0.wireOp",EDGE,"E4.2"),sQuery(id+"F0.wireOp",EDGE,"E4.3"),sQuery(id+"F0.wireOp",EDGE,"E4.4"),sQuery(id+"F0.wireOp",EDGE,"E4.5"),sQuery(id+"F0.wireOp",EDGE,"E5.0"),sQuery(id+"F0.wireOp",EDGE,"E5.1"),sQuery(id+"F0.wireOp",EDGE,"E5.2"),sQuery(id+"F0.wireOp",EDGE,"E5.3"),sQuery(id+"F0.wireOp",EDGE,"E5.4"),sQuery(id+"F0.wireOp",EDGE,"E5.5"),sQuery(id+"F0.wireOp",EDGE,"E6.0"),sQuery(id+"F0.wireOp",EDGE,"E6.1"),sQuery(id+"F0.wireOp",EDGE,"E6.2"),sQuery(id+"F0.wireOp",EDGE,"E6.3"),sQuery(id+"F0.wireOp",EDGE,"E6.4"),sQuery(id+"F0.wireOp",EDGE,"E6.5"),sQuery(id+"F0.wireOp",EDGE,"E7"),sQuery(id+"F0.wireOp",EDGE,"E8"),sQuery(id+"F0.wireOp",EDGE,"E9"),sQuery(id+"F0.wireOp",EDGE,"E10"),sQuery(id+"F0.wireOp",EDGE,"E12"),sQuery(id+"F0.wireOp",EDGE,"E13"),sQuery(id+"F0.wireOp",EDGE,"E14")])],"isStart":true}),makeQuery(id+"F3.opExtrude","SWEPT_FACE",FACE,{"disambiguationData":[OSD([sQuery(id+"F2.wireOp",EDGE,"E19.2")])]})]});
            var Q44;
            Q44=makeQuery(id+"F3.boolean.opBoolean","INTERSECT",EDGE,{"derivedFrom":[makeQuery(id+"F1.opExtrude","CAP_FACE",FACE,{"disambiguationData":[OSD([sQuery(id+"F0.wireOp",EDGE,"E4.0"),sQuery(id+"F0.wireOp",EDGE,"E4.1"),sQuery(id+"F0.wireOp",EDGE,"E4.2"),sQuery(id+"F0.wireOp",EDGE,"E4.3"),sQuery(id+"F0.wireOp",EDGE,"E4.4"),sQuery(id+"F0.wireOp",EDGE,"E4.5"),sQuery(id+"F0.wireOp",EDGE,"E5.0"),sQuery(id+"F0.wireOp",EDGE,"E5.1"),sQuery(id+"F0.wireOp",EDGE,"E5.2"),sQuery(id+"F0.wireOp",EDGE,"E5.3"),sQuery(id+"F0.wireOp",EDGE,"E5.4"),sQuery(id+"F0.wireOp",EDGE,"E5.5"),sQuery(id+"F0.wireOp",EDGE,"E6.0"),sQuery(id+"F0.wireOp",EDGE,"E6.1"),sQuery(id+"F0.wireOp",EDGE,"E6.2"),sQuery(id+"F0.wireOp",EDGE,"E6.3"),sQuery(id+"F0.wireOp",EDGE,"E6.4"),sQuery(id+"F0.wireOp",EDGE,"E6.5"),sQuery(id+"F0.wireOp",EDGE,"E7"),sQuery(id+"F0.wireOp",EDGE,"E8"),sQuery(id+"F0.wireOp",EDGE,"E9"),sQuery(id+"F0.wireOp",EDGE,"E10"),sQuery(id+"F0.wireOp",EDGE,"E12"),sQuery(id+"F0.wireOp",EDGE,"E13"),sQuery(id+"F0.wireOp",EDGE,"E14")])],"isStart":true}),makeQuery(id+"F3.opExtrude","SWEPT_FACE",FACE,{"disambiguationData":[OSD([sQuery(id+"F2.wireOp",EDGE,"E37")])]})]});
            var Q45;
            Q45=makeQuery(id+"F3.boolean.opBoolean","INTERSECT",EDGE,{"derivedFrom":[makeQuery(id+"F1.opExtrude","CAP_FACE",FACE,{"disambiguationData":[OSD([sQuery(id+"F0.wireOp",EDGE,"E4.0"),sQuery(id+"F0.wireOp",EDGE,"E4.1"),sQuery(id+"F0.wireOp",EDGE,"E4.2"),sQuery(id+"F0.wireOp",EDGE,"E4.3"),sQuery(id+"F0.wireOp",EDGE,"E4.4"),sQuery(id+"F0.wireOp",EDGE,"E4.5"),sQuery(id+"F0.wireOp",EDGE,"E5.0"),sQuery(id+"F0.wireOp",EDGE,"E5.1"),sQuery(id+"F0.wireOp",EDGE,"E5.2"),sQuery(id+"F0.wireOp",EDGE,"E5.3"),sQuery(id+"F0.wireOp",EDGE,"E5.4"),sQuery(id+"F0.wireOp",EDGE,"E5.5"),sQuery(id+"F0.wireOp",EDGE,"E6.0"),sQuery(id+"F0.wireOp",EDGE,"E6.1"),sQuery(id+"F0.wireOp",EDGE,"E6.2"),sQuery(id+"F0.wireOp",EDGE,"E6.3"),sQuery(id+"F0.wireOp",EDGE,"E6.4"),sQuery(id+"F0.wireOp",EDGE,"E6.5"),sQuery(id+"F0.wireOp",EDGE,"E7"),sQuery(id+"F0.wireOp",EDGE,"E8"),sQuery(id+"F0.wireOp",EDGE,"E9"),sQuery(id+"F0.wireOp",EDGE,"E10"),sQuery(id+"F0.wireOp",EDGE,"E12"),sQuery(id+"F0.wireOp",EDGE,"E13"),sQuery(id+"F0.wireOp",EDGE,"E14")])],"isStart":true}),makeQuery(id+"F3.opExtrude","SWEPT_FACE",FACE,{"disambiguationData":[OSD([sQuery(id+"F2.wireOp",EDGE,"E31.0")])]})]});
            var Q46;
            Q46=makeQuery(id+"F3.boolean.opBoolean","INTERSECT",EDGE,{"derivedFrom":[makeQuery(id+"F1.opExtrude","CAP_FACE",FACE,{"disambiguationData":[OSD([sQuery(id+"F0.wireOp",EDGE,"E4.0"),sQuery(id+"F0.wireOp",EDGE,"E4.1"),sQuery(id+"F0.wireOp",EDGE,"E4.2"),sQuery(id+"F0.wireOp",EDGE,"E4.3"),sQuery(id+"F0.wireOp",EDGE,"E4.4"),sQuery(id+"F0.wireOp",EDGE,"E4.5"),sQuery(id+"F0.wireOp",EDGE,"E5.0"),sQuery(id+"F0.wireOp",EDGE,"E5.1"),sQuery(id+"F0.wireOp",EDGE,"E5.2"),sQuery(id+"F0.wireOp",EDGE,"E5.3"),sQuery(id+"F0.wireOp",EDGE,"E5.4"),sQuery(id+"F0.wireOp",EDGE,"E5.5"),sQuery(id+"F0.wireOp",EDGE,"E6.0"),sQuery(id+"F0.wireOp",EDGE,"E6.1"),sQuery(id+"F0.wireOp",EDGE,"E6.2"),sQuery(id+"F0.wireOp",EDGE,"E6.3"),sQuery(id+"F0.wireOp",EDGE,"E6.4"),sQuery(id+"F0.wireOp",EDGE,"E6.5"),sQuery(id+"F0.wireOp",EDGE,"E7"),sQuery(id+"F0.wireOp",EDGE,"E8"),sQuery(id+"F0.wireOp",EDGE,"E9"),sQuery(id+"F0.wireOp",EDGE,"E10"),sQuery(id+"F0.wireOp",EDGE,"E12"),sQuery(id+"F0.wireOp",EDGE,"E13"),sQuery(id+"F0.wireOp",EDGE,"E14")])],"isStart":true}),makeQuery(id+"F3.opExtrude","SWEPT_FACE",FACE,{"disambiguationData":[OSD([sQuery(id+"F2.wireOp",EDGE,"E39")])]})]});
            var Q47;
            Q47=makeQuery(id+"F3.boolean.opBoolean","INTERSECT",EDGE,{"derivedFrom":[makeQuery(id+"F1.opExtrude","CAP_FACE",FACE,{"disambiguationData":[OSD([sQuery(id+"F0.wireOp",EDGE,"E4.0"),sQuery(id+"F0.wireOp",EDGE,"E4.1"),sQuery(id+"F0.wireOp",EDGE,"E4.2"),sQuery(id+"F0.wireOp",EDGE,"E4.3"),sQuery(id+"F0.wireOp",EDGE,"E4.4"),sQuery(id+"F0.wireOp",EDGE,"E4.5"),sQuery(id+"F0.wireOp",EDGE,"E5.0"),sQuery(id+"F0.wireOp",EDGE,"E5.1"),sQuery(id+"F0.wireOp",EDGE,"E5.2"),sQuery(id+"F0.wireOp",EDGE,"E5.3"),sQuery(id+"F0.wireOp",EDGE,"E5.4"),sQuery(id+"F0.wireOp",EDGE,"E5.5"),sQuery(id+"F0.wireOp",EDGE,"E6.0"),sQuery(id+"F0.wireOp",EDGE,"E6.1"),sQuery(id+"F0.wireOp",EDGE,"E6.2"),sQuery(id+"F0.wireOp",EDGE,"E6.3"),sQuery(id+"F0.wireOp",EDGE,"E6.4"),sQuery(id+"F0.wireOp",EDGE,"E6.5"),sQuery(id+"F0.wireOp",EDGE,"E7"),sQuery(id+"F0.wireOp",EDGE,"E8"),sQuery(id+"F0.wireOp",EDGE,"E9"),sQuery(id+"F0.wireOp",EDGE,"E10"),sQuery(id+"F0.wireOp",EDGE,"E12"),sQuery(id+"F0.wireOp",EDGE,"E13"),sQuery(id+"F0.wireOp",EDGE,"E14")])],"isStart":true}),makeQuery(id+"F3.opExtrude","SWEPT_FACE",FACE,{"disambiguationData":[OSD([sQuery(id+"F2.wireOp",EDGE,"E42.trimOffspring")])]})]});
            var Q48;
            Q48=makeQuery(id+"F3.boolean.opBoolean","INTERSECT",EDGE,{"derivedFrom":[makeQuery(id+"F1.opExtrude","CAP_FACE",FACE,{"disambiguationData":[OSD([sQuery(id+"F0.wireOp",EDGE,"E4.0"),sQuery(id+"F0.wireOp",EDGE,"E4.1"),sQuery(id+"F0.wireOp",EDGE,"E4.2"),sQuery(id+"F0.wireOp",EDGE,"E4.3"),sQuery(id+"F0.wireOp",EDGE,"E4.4"),sQuery(id+"F0.wireOp",EDGE,"E4.5"),sQuery(id+"F0.wireOp",EDGE,"E5.0"),sQuery(id+"F0.wireOp",EDGE,"E5.1"),sQuery(id+"F0.wireOp",EDGE,"E5.2"),sQuery(id+"F0.wireOp",EDGE,"E5.3"),sQuery(id+"F0.wireOp",EDGE,"E5.4"),sQuery(id+"F0.wireOp",EDGE,"E5.5"),sQuery(id+"F0.wireOp",EDGE,"E6.0"),sQuery(id+"F0.wireOp",EDGE,"E6.1"),sQuery(id+"F0.wireOp",EDGE,"E6.2"),sQuery(id+"F0.wireOp",EDGE,"E6.3"),sQuery(id+"F0.wireOp",EDGE,"E6.4"),sQuery(id+"F0.wireOp",EDGE,"E6.5"),sQuery(id+"F0.wireOp",EDGE,"E7"),sQuery(id+"F0.wireOp",EDGE,"E8"),sQuery(id+"F0.wireOp",EDGE,"E9"),sQuery(id+"F0.wireOp",EDGE,"E10"),sQuery(id+"F0.wireOp",EDGE,"E12"),sQuery(id+"F0.wireOp",EDGE,"E13"),sQuery(id+"F0.wireOp",EDGE,"E14")])],"isStart":true}),makeQuery(id+"F3.opExtrude","SWEPT_FACE",FACE,{"disambiguationData":[OSD([sQuery(id+"F2.wireOp",EDGE,"E27.trimOffspring")])]})]});
            var Q49;
            Q49=makeQuery(id+"F3.boolean.opBoolean","INTERSECT",EDGE,{"derivedFrom":[makeQuery(id+"F1.opExtrude","CAP_FACE",FACE,{"disambiguationData":[OSD([sQuery(id+"F0.wireOp",EDGE,"E4.0"),sQuery(id+"F0.wireOp",EDGE,"E4.1"),sQuery(id+"F0.wireOp",EDGE,"E4.2"),sQuery(id+"F0.wireOp",EDGE,"E4.3"),sQuery(id+"F0.wireOp",EDGE,"E4.4"),sQuery(id+"F0.wireOp",EDGE,"E4.5"),sQuery(id+"F0.wireOp",EDGE,"E5.0"),sQuery(id+"F0.wireOp",EDGE,"E5.1"),sQuery(id+"F0.wireOp",EDGE,"E5.2"),sQuery(id+"F0.wireOp",EDGE,"E5.3"),sQuery(id+"F0.wireOp",EDGE,"E5.4"),sQuery(id+"F0.wireOp",EDGE,"E5.5"),sQuery(id+"F0.wireOp",EDGE,"E6.0"),sQuery(id+"F0.wireOp",EDGE,"E6.1"),sQuery(id+"F0.wireOp",EDGE,"E6.2"),sQuery(id+"F0.wireOp",EDGE,"E6.3"),sQuery(id+"F0.wireOp",EDGE,"E6.4"),sQuery(id+"F0.wireOp",EDGE,"E6.5"),sQuery(id+"F0.wireOp",EDGE,"E7"),sQuery(id+"F0.wireOp",EDGE,"E8"),sQuery(id+"F0.wireOp",EDGE,"E9"),sQuery(id+"F0.wireOp",EDGE,"E10"),sQuery(id+"F0.wireOp",EDGE,"E12"),sQuery(id+"F0.wireOp",EDGE,"E13"),sQuery(id+"F0.wireOp",EDGE,"E14")])],"isStart":true}),makeQuery(id+"F3.opExtrude","SWEPT_FACE",FACE,{"disambiguationData":[OSD([sQuery(id+"F2.wireOp",EDGE,"E24.0")])]})]});
            var Q50;
            Q50=makeQuery(id+"F3.boolean.opBoolean","INTERSECT",EDGE,{"derivedFrom":[makeQuery(id+"F1.opExtrude","CAP_FACE",FACE,{"disambiguationData":[OSD([sQuery(id+"F0.wireOp",EDGE,"E4.0"),sQuery(id+"F0.wireOp",EDGE,"E4.1"),sQuery(id+"F0.wireOp",EDGE,"E4.2"),sQuery(id+"F0.wireOp",EDGE,"E4.3"),sQuery(id+"F0.wireOp",EDGE,"E4.4"),sQuery(id+"F0.wireOp",EDGE,"E4.5"),sQuery(id+"F0.wireOp",EDGE,"E5.0"),sQuery(id+"F0.wireOp",EDGE,"E5.1"),sQuery(id+"F0.wireOp",EDGE,"E5.2"),sQuery(id+"F0.wireOp",EDGE,"E5.3"),sQuery(id+"F0.wireOp",EDGE,"E5.4"),sQuery(id+"F0.wireOp",EDGE,"E5.5"),sQuery(id+"F0.wireOp",EDGE,"E6.0"),sQuery(id+"F0.wireOp",EDGE,"E6.1"),sQuery(id+"F0.wireOp",EDGE,"E6.2"),sQuery(id+"F0.wireOp",EDGE,"E6.3"),sQuery(id+"F0.wireOp",EDGE,"E6.4"),sQuery(id+"F0.wireOp",EDGE,"E6.5"),sQuery(id+"F0.wireOp",EDGE,"E7"),sQuery(id+"F0.wireOp",EDGE,"E8"),sQuery(id+"F0.wireOp",EDGE,"E9"),sQuery(id+"F0.wireOp",EDGE,"E10"),sQuery(id+"F0.wireOp",EDGE,"E12"),sQuery(id+"F0.wireOp",EDGE,"E13"),sQuery(id+"F0.wireOp",EDGE,"E14")])],"isStart":true}),makeQuery(id+"F3.opExtrude","SWEPT_FACE",FACE,{"disambiguationData":[OSD([sQuery(id+"F2.wireOp",EDGE,"E23.0")])]})]});
            var Q51;
            Q51=makeQuery(id+"F3.boolean.opBoolean","INTERSECT",EDGE,{"derivedFrom":[makeQuery(id+"F1.opExtrude","CAP_FACE",FACE,{"disambiguationData":[OSD([sQuery(id+"F0.wireOp",EDGE,"E4.0"),sQuery(id+"F0.wireOp",EDGE,"E4.1"),sQuery(id+"F0.wireOp",EDGE,"E4.2"),sQuery(id+"F0.wireOp",EDGE,"E4.3"),sQuery(id+"F0.wireOp",EDGE,"E4.4"),sQuery(id+"F0.wireOp",EDGE,"E4.5"),sQuery(id+"F0.wireOp",EDGE,"E5.0"),sQuery(id+"F0.wireOp",EDGE,"E5.1"),sQuery(id+"F0.wireOp",EDGE,"E5.2"),sQuery(id+"F0.wireOp",EDGE,"E5.3"),sQuery(id+"F0.wireOp",EDGE,"E5.4"),sQuery(id+"F0.wireOp",EDGE,"E5.5"),sQuery(id+"F0.wireOp",EDGE,"E6.0"),sQuery(id+"F0.wireOp",EDGE,"E6.1"),sQuery(id+"F0.wireOp",EDGE,"E6.2"),sQuery(id+"F0.wireOp",EDGE,"E6.3"),sQuery(id+"F0.wireOp",EDGE,"E6.4"),sQuery(id+"F0.wireOp",EDGE,"E6.5"),sQuery(id+"F0.wireOp",EDGE,"E7"),sQuery(id+"F0.wireOp",EDGE,"E8"),sQuery(id+"F0.wireOp",EDGE,"E9"),sQuery(id+"F0.wireOp",EDGE,"E10"),sQuery(id+"F0.wireOp",EDGE,"E12"),sQuery(id+"F0.wireOp",EDGE,"E13"),sQuery(id+"F0.wireOp",EDGE,"E14")])],"isStart":true}),makeQuery(id+"F3.opExtrude","SWEPT_FACE",FACE,{"disambiguationData":[OSD([sQuery(id+"F2.wireOp",EDGE,"E23.1")])]})]});
            var Q52;
            Q52=makeQuery(id+"F3.boolean.opBoolean","INTERSECT",EDGE,{"derivedFrom":[makeQuery(id+"F1.opExtrude","CAP_FACE",FACE,{"disambiguationData":[OSD([sQuery(id+"F0.wireOp",EDGE,"E4.0"),sQuery(id+"F0.wireOp",EDGE,"E4.1"),sQuery(id+"F0.wireOp",EDGE,"E4.2"),sQuery(id+"F0.wireOp",EDGE,"E4.3"),sQuery(id+"F0.wireOp",EDGE,"E4.4"),sQuery(id+"F0.wireOp",EDGE,"E4.5"),sQuery(id+"F0.wireOp",EDGE,"E5.0"),sQuery(id+"F0.wireOp",EDGE,"E5.1"),sQuery(id+"F0.wireOp",EDGE,"E5.2"),sQuery(id+"F0.wireOp",EDGE,"E5.3"),sQuery(id+"F0.wireOp",EDGE,"E5.4"),sQuery(id+"F0.wireOp",EDGE,"E5.5"),sQuery(id+"F0.wireOp",EDGE,"E6.0"),sQuery(id+"F0.wireOp",EDGE,"E6.1"),sQuery(id+"F0.wireOp",EDGE,"E6.2"),sQuery(id+"F0.wireOp",EDGE,"E6.3"),sQuery(id+"F0.wireOp",EDGE,"E6.4"),sQuery(id+"F0.wireOp",EDGE,"E6.5"),sQuery(id+"F0.wireOp",EDGE,"E7"),sQuery(id+"F0.wireOp",EDGE,"E8"),sQuery(id+"F0.wireOp",EDGE,"E9"),sQuery(id+"F0.wireOp",EDGE,"E10"),sQuery(id+"F0.wireOp",EDGE,"E12"),sQuery(id+"F0.wireOp",EDGE,"E13"),sQuery(id+"F0.wireOp",EDGE,"E14")])],"isStart":true}),makeQuery(id+"F3.opExtrude","SWEPT_FACE",FACE,{"disambiguationData":[OSD([sQuery(id+"F2.wireOp",EDGE,"E22.1")])]})]});
            var Q53;
            Q53=makeQuery(id+"F3.boolean.opBoolean","INTERSECT",EDGE,{"derivedFrom":[makeQuery(id+"F1.opExtrude","CAP_FACE",FACE,{"disambiguationData":[OSD([sQuery(id+"F0.wireOp",EDGE,"E4.0"),sQuery(id+"F0.wireOp",EDGE,"E4.1"),sQuery(id+"F0.wireOp",EDGE,"E4.2"),sQuery(id+"F0.wireOp",EDGE,"E4.3"),sQuery(id+"F0.wireOp",EDGE,"E4.4"),sQuery(id+"F0.wireOp",EDGE,"E4.5"),sQuery(id+"F0.wireOp",EDGE,"E5.0"),sQuery(id+"F0.wireOp",EDGE,"E5.1"),sQuery(id+"F0.wireOp",EDGE,"E5.2"),sQuery(id+"F0.wireOp",EDGE,"E5.3"),sQuery(id+"F0.wireOp",EDGE,"E5.4"),sQuery(id+"F0.wireOp",EDGE,"E5.5"),sQuery(id+"F0.wireOp",EDGE,"E6.0"),sQuery(id+"F0.wireOp",EDGE,"E6.1"),sQuery(id+"F0.wireOp",EDGE,"E6.2"),sQuery(id+"F0.wireOp",EDGE,"E6.3"),sQuery(id+"F0.wireOp",EDGE,"E6.4"),sQuery(id+"F0.wireOp",EDGE,"E6.5"),sQuery(id+"F0.wireOp",EDGE,"E7"),sQuery(id+"F0.wireOp",EDGE,"E8"),sQuery(id+"F0.wireOp",EDGE,"E9"),sQuery(id+"F0.wireOp",EDGE,"E10"),sQuery(id+"F0.wireOp",EDGE,"E12"),sQuery(id+"F0.wireOp",EDGE,"E13"),sQuery(id+"F0.wireOp",EDGE,"E14")])],"isStart":true}),makeQuery(id+"F3.opExtrude","SWEPT_FACE",FACE,{"disambiguationData":[OSD([sQuery(id+"F2.wireOp",EDGE,"E22.0")])]})]});
            var Q54;
            Q54=makeQuery(id+"F3.boolean.opBoolean","INTERSECT",EDGE,{"derivedFrom":[makeQuery(id+"F1.opExtrude","CAP_FACE",FACE,{"disambiguationData":[OSD([sQuery(id+"F0.wireOp",EDGE,"E4.0"),sQuery(id+"F0.wireOp",EDGE,"E4.1"),sQuery(id+"F0.wireOp",EDGE,"E4.2"),sQuery(id+"F0.wireOp",EDGE,"E4.3"),sQuery(id+"F0.wireOp",EDGE,"E4.4"),sQuery(id+"F0.wireOp",EDGE,"E4.5"),sQuery(id+"F0.wireOp",EDGE,"E5.0"),sQuery(id+"F0.wireOp",EDGE,"E5.1"),sQuery(id+"F0.wireOp",EDGE,"E5.2"),sQuery(id+"F0.wireOp",EDGE,"E5.3"),sQuery(id+"F0.wireOp",EDGE,"E5.4"),sQuery(id+"F0.wireOp",EDGE,"E5.5"),sQuery(id+"F0.wireOp",EDGE,"E6.0"),sQuery(id+"F0.wireOp",EDGE,"E6.1"),sQuery(id+"F0.wireOp",EDGE,"E6.2"),sQuery(id+"F0.wireOp",EDGE,"E6.3"),sQuery(id+"F0.wireOp",EDGE,"E6.4"),sQuery(id+"F0.wireOp",EDGE,"E6.5"),sQuery(id+"F0.wireOp",EDGE,"E7"),sQuery(id+"F0.wireOp",EDGE,"E8"),sQuery(id+"F0.wireOp",EDGE,"E9"),sQuery(id+"F0.wireOp",EDGE,"E10"),sQuery(id+"F0.wireOp",EDGE,"E12"),sQuery(id+"F0.wireOp",EDGE,"E13"),sQuery(id+"F0.wireOp",EDGE,"E14")])],"isStart":true}),makeQuery(id+"F3.opExtrude","SWEPT_FACE",FACE,{"disambiguationData":[OSD([sQuery(id+"F2.wireOp",EDGE,"E24.1")])]})]});
            var Q55;
            Q55=makeQuery(id+"F3.boolean.opBoolean","INTERSECT",EDGE,{"derivedFrom":[makeQuery(id+"F1.opExtrude","CAP_FACE",FACE,{"disambiguationData":[OSD([sQuery(id+"F0.wireOp",EDGE,"E4.0"),sQuery(id+"F0.wireOp",EDGE,"E4.1"),sQuery(id+"F0.wireOp",EDGE,"E4.2"),sQuery(id+"F0.wireOp",EDGE,"E4.3"),sQuery(id+"F0.wireOp",EDGE,"E4.4"),sQuery(id+"F0.wireOp",EDGE,"E4.5"),sQuery(id+"F0.wireOp",EDGE,"E5.0"),sQuery(id+"F0.wireOp",EDGE,"E5.1"),sQuery(id+"F0.wireOp",EDGE,"E5.2"),sQuery(id+"F0.wireOp",EDGE,"E5.3"),sQuery(id+"F0.wireOp",EDGE,"E5.4"),sQuery(id+"F0.wireOp",EDGE,"E5.5"),sQuery(id+"F0.wireOp",EDGE,"E6.0"),sQuery(id+"F0.wireOp",EDGE,"E6.1"),sQuery(id+"F0.wireOp",EDGE,"E6.2"),sQuery(id+"F0.wireOp",EDGE,"E6.3"),sQuery(id+"F0.wireOp",EDGE,"E6.4"),sQuery(id+"F0.wireOp",EDGE,"E6.5"),sQuery(id+"F0.wireOp",EDGE,"E7"),sQuery(id+"F0.wireOp",EDGE,"E8"),sQuery(id+"F0.wireOp",EDGE,"E9"),sQuery(id+"F0.wireOp",EDGE,"E10"),sQuery(id+"F0.wireOp",EDGE,"E12"),sQuery(id+"F0.wireOp",EDGE,"E13"),sQuery(id+"F0.wireOp",EDGE,"E14")])],"isStart":true}),makeQuery(id+"F3.opExtrude","SWEPT_FACE",FACE,{"disambiguationData":[OSD([sQuery(id+"F2.wireOp",EDGE,"E28.trimOffspring")])]})]});
            var Q56;
            Q56=makeQuery(id+"F3.boolean.opBoolean","INTERSECT",EDGE,{"derivedFrom":[makeQuery(id+"F1.opExtrude","CAP_FACE",FACE,{"disambiguationData":[OSD([sQuery(id+"F0.wireOp",EDGE,"E4.0"),sQuery(id+"F0.wireOp",EDGE,"E4.1"),sQuery(id+"F0.wireOp",EDGE,"E4.2"),sQuery(id+"F0.wireOp",EDGE,"E4.3"),sQuery(id+"F0.wireOp",EDGE,"E4.4"),sQuery(id+"F0.wireOp",EDGE,"E4.5"),sQuery(id+"F0.wireOp",EDGE,"E5.0"),sQuery(id+"F0.wireOp",EDGE,"E5.1"),sQuery(id+"F0.wireOp",EDGE,"E5.2"),sQuery(id+"F0.wireOp",EDGE,"E5.3"),sQuery(id+"F0.wireOp",EDGE,"E5.4"),sQuery(id+"F0.wireOp",EDGE,"E5.5"),sQuery(id+"F0.wireOp",EDGE,"E6.0"),sQuery(id+"F0.wireOp",EDGE,"E6.1"),sQuery(id+"F0.wireOp",EDGE,"E6.2"),sQuery(id+"F0.wireOp",EDGE,"E6.3"),sQuery(id+"F0.wireOp",EDGE,"E6.4"),sQuery(id+"F0.wireOp",EDGE,"E6.5"),sQuery(id+"F0.wireOp",EDGE,"E7"),sQuery(id+"F0.wireOp",EDGE,"E8"),sQuery(id+"F0.wireOp",EDGE,"E9"),sQuery(id+"F0.wireOp",EDGE,"E10"),sQuery(id+"F0.wireOp",EDGE,"E12"),sQuery(id+"F0.wireOp",EDGE,"E13"),sQuery(id+"F0.wireOp",EDGE,"E14")])],"isStart":true}),makeQuery(id+"F3.opExtrude","SWEPT_FACE",FACE,{"disambiguationData":[OSD([sQuery(id+"F2.wireOp",EDGE,"E19.0")])]})]});
            var Q57;
            Q57=makeQuery(id+"F3.boolean.opBoolean","INTERSECT",EDGE,{"derivedFrom":[makeQuery(id+"F1.opExtrude","CAP_FACE",FACE,{"disambiguationData":[OSD([sQuery(id+"F0.wireOp",EDGE,"E4.0"),sQuery(id+"F0.wireOp",EDGE,"E4.1"),sQuery(id+"F0.wireOp",EDGE,"E4.2"),sQuery(id+"F0.wireOp",EDGE,"E4.3"),sQuery(id+"F0.wireOp",EDGE,"E4.4"),sQuery(id+"F0.wireOp",EDGE,"E4.5"),sQuery(id+"F0.wireOp",EDGE,"E5.0"),sQuery(id+"F0.wireOp",EDGE,"E5.1"),sQuery(id+"F0.wireOp",EDGE,"E5.2"),sQuery(id+"F0.wireOp",EDGE,"E5.3"),sQuery(id+"F0.wireOp",EDGE,"E5.4"),sQuery(id+"F0.wireOp",EDGE,"E5.5"),sQuery(id+"F0.wireOp",EDGE,"E6.0"),sQuery(id+"F0.wireOp",EDGE,"E6.1"),sQuery(id+"F0.wireOp",EDGE,"E6.2"),sQuery(id+"F0.wireOp",EDGE,"E6.3"),sQuery(id+"F0.wireOp",EDGE,"E6.4"),sQuery(id+"F0.wireOp",EDGE,"E6.5"),sQuery(id+"F0.wireOp",EDGE,"E7"),sQuery(id+"F0.wireOp",EDGE,"E8"),sQuery(id+"F0.wireOp",EDGE,"E9"),sQuery(id+"F0.wireOp",EDGE,"E10"),sQuery(id+"F0.wireOp",EDGE,"E12"),sQuery(id+"F0.wireOp",EDGE,"E13"),sQuery(id+"F0.wireOp",EDGE,"E14")])],"isStart":true}),makeQuery(id+"F3.opExtrude","SWEPT_FACE",FACE,{"disambiguationData":[OSD([sQuery(id+"F2.wireOp",EDGE,"E41.trimOffspring")])]})]});
            var Q58;
            Q58=makeQuery(id+"F3.boolean.opBoolean","INTERSECT",EDGE,{"derivedFrom":[makeQuery(id+"F1.opExtrude","CAP_FACE",FACE,{"disambiguationData":[OSD([sQuery(id+"F0.wireOp",EDGE,"E4.0"),sQuery(id+"F0.wireOp",EDGE,"E4.1"),sQuery(id+"F0.wireOp",EDGE,"E4.2"),sQuery(id+"F0.wireOp",EDGE,"E4.3"),sQuery(id+"F0.wireOp",EDGE,"E4.4"),sQuery(id+"F0.wireOp",EDGE,"E4.5"),sQuery(id+"F0.wireOp",EDGE,"E5.0"),sQuery(id+"F0.wireOp",EDGE,"E5.1"),sQuery(id+"F0.wireOp",EDGE,"E5.2"),sQuery(id+"F0.wireOp",EDGE,"E5.3"),sQuery(id+"F0.wireOp",EDGE,"E5.4"),sQuery(id+"F0.wireOp",EDGE,"E5.5"),sQuery(id+"F0.wireOp",EDGE,"E6.0"),sQuery(id+"F0.wireOp",EDGE,"E6.1"),sQuery(id+"F0.wireOp",EDGE,"E6.2"),sQuery(id+"F0.wireOp",EDGE,"E6.3"),sQuery(id+"F0.wireOp",EDGE,"E6.4"),sQuery(id+"F0.wireOp",EDGE,"E6.5"),sQuery(id+"F0.wireOp",EDGE,"E7"),sQuery(id+"F0.wireOp",EDGE,"E8"),sQuery(id+"F0.wireOp",EDGE,"E9"),sQuery(id+"F0.wireOp",EDGE,"E10"),sQuery(id+"F0.wireOp",EDGE,"E12"),sQuery(id+"F0.wireOp",EDGE,"E13"),sQuery(id+"F0.wireOp",EDGE,"E14")])],"isStart":true}),makeQuery(id+"F3.opExtrude","SWEPT_FACE",FACE,{"disambiguationData":[OSD([sQuery(id+"F2.wireOp",EDGE,"E40.trimOffspring")])]})]});
            var Q59;
            Q59=makeQuery(id+"F3.boolean.opBoolean","INTERSECT",EDGE,{"derivedFrom":[makeQuery(id+"F1.opExtrude","CAP_FACE",FACE,{"disambiguationData":[OSD([sQuery(id+"F0.wireOp",EDGE,"E4.0"),sQuery(id+"F0.wireOp",EDGE,"E4.1"),sQuery(id+"F0.wireOp",EDGE,"E4.2"),sQuery(id+"F0.wireOp",EDGE,"E4.3"),sQuery(id+"F0.wireOp",EDGE,"E4.4"),sQuery(id+"F0.wireOp",EDGE,"E4.5"),sQuery(id+"F0.wireOp",EDGE,"E5.0"),sQuery(id+"F0.wireOp",EDGE,"E5.1"),sQuery(id+"F0.wireOp",EDGE,"E5.2"),sQuery(id+"F0.wireOp",EDGE,"E5.3"),sQuery(id+"F0.wireOp",EDGE,"E5.4"),sQuery(id+"F0.wireOp",EDGE,"E5.5"),sQuery(id+"F0.wireOp",EDGE,"E6.0"),sQuery(id+"F0.wireOp",EDGE,"E6.1"),sQuery(id+"F0.wireOp",EDGE,"E6.2"),sQuery(id+"F0.wireOp",EDGE,"E6.3"),sQuery(id+"F0.wireOp",EDGE,"E6.4"),sQuery(id+"F0.wireOp",EDGE,"E6.5"),sQuery(id+"F0.wireOp",EDGE,"E7"),sQuery(id+"F0.wireOp",EDGE,"E8"),sQuery(id+"F0.wireOp",EDGE,"E9"),sQuery(id+"F0.wireOp",EDGE,"E10"),sQuery(id+"F0.wireOp",EDGE,"E12"),sQuery(id+"F0.wireOp",EDGE,"E13"),sQuery(id+"F0.wireOp",EDGE,"E14")])],"isStart":true}),makeQuery(id+"F3.opExtrude","SWEPT_FACE",FACE,{"disambiguationData":[OSD([sQuery(id+"F2.wireOp",EDGE,"E19.3")])]})]});
            var Q60;
            Q60=makeQuery(id+"F3.boolean.opBoolean","INTERSECT",EDGE,{"derivedFrom":[makeQuery(id+"F1.opExtrude","CAP_FACE",FACE,{"disambiguationData":[OSD([sQuery(id+"F0.wireOp",EDGE,"E4.0"),sQuery(id+"F0.wireOp",EDGE,"E4.1"),sQuery(id+"F0.wireOp",EDGE,"E4.2"),sQuery(id+"F0.wireOp",EDGE,"E4.3"),sQuery(id+"F0.wireOp",EDGE,"E4.4"),sQuery(id+"F0.wireOp",EDGE,"E4.5"),sQuery(id+"F0.wireOp",EDGE,"E5.0"),sQuery(id+"F0.wireOp",EDGE,"E5.1"),sQuery(id+"F0.wireOp",EDGE,"E5.2"),sQuery(id+"F0.wireOp",EDGE,"E5.3"),sQuery(id+"F0.wireOp",EDGE,"E5.4"),sQuery(id+"F0.wireOp",EDGE,"E5.5"),sQuery(id+"F0.wireOp",EDGE,"E6.0"),sQuery(id+"F0.wireOp",EDGE,"E6.1"),sQuery(id+"F0.wireOp",EDGE,"E6.2"),sQuery(id+"F0.wireOp",EDGE,"E6.3"),sQuery(id+"F0.wireOp",EDGE,"E6.4"),sQuery(id+"F0.wireOp",EDGE,"E6.5"),sQuery(id+"F0.wireOp",EDGE,"E7"),sQuery(id+"F0.wireOp",EDGE,"E8"),sQuery(id+"F0.wireOp",EDGE,"E9"),sQuery(id+"F0.wireOp",EDGE,"E10"),sQuery(id+"F0.wireOp",EDGE,"E12"),sQuery(id+"F0.wireOp",EDGE,"E13"),sQuery(id+"F0.wireOp",EDGE,"E14")])],"isStart":true}),makeQuery(id+"F3.opExtrude","SWEPT_FACE",FACE,{"disambiguationData":[OSD([sQuery(id+"F2.wireOp",EDGE,"E21.trimOffspring")])]})]});
            var Q61;
            Q61=makeQuery(id+"F3.boolean.opBoolean","INTERSECT",EDGE,{"derivedFrom":[makeQuery(id+"F1.opExtrude","CAP_FACE",FACE,{"disambiguationData":[OSD([sQuery(id+"F0.wireOp",EDGE,"E4.0"),sQuery(id+"F0.wireOp",EDGE,"E4.1"),sQuery(id+"F0.wireOp",EDGE,"E4.2"),sQuery(id+"F0.wireOp",EDGE,"E4.3"),sQuery(id+"F0.wireOp",EDGE,"E4.4"),sQuery(id+"F0.wireOp",EDGE,"E4.5"),sQuery(id+"F0.wireOp",EDGE,"E5.0"),sQuery(id+"F0.wireOp",EDGE,"E5.1"),sQuery(id+"F0.wireOp",EDGE,"E5.2"),sQuery(id+"F0.wireOp",EDGE,"E5.3"),sQuery(id+"F0.wireOp",EDGE,"E5.4"),sQuery(id+"F0.wireOp",EDGE,"E5.5"),sQuery(id+"F0.wireOp",EDGE,"E6.0"),sQuery(id+"F0.wireOp",EDGE,"E6.1"),sQuery(id+"F0.wireOp",EDGE,"E6.2"),sQuery(id+"F0.wireOp",EDGE,"E6.3"),sQuery(id+"F0.wireOp",EDGE,"E6.4"),sQuery(id+"F0.wireOp",EDGE,"E6.5"),sQuery(id+"F0.wireOp",EDGE,"E7"),sQuery(id+"F0.wireOp",EDGE,"E8"),sQuery(id+"F0.wireOp",EDGE,"E9"),sQuery(id+"F0.wireOp",EDGE,"E10"),sQuery(id+"F0.wireOp",EDGE,"E12"),sQuery(id+"F0.wireOp",EDGE,"E13"),sQuery(id+"F0.wireOp",EDGE,"E14")])],"isStart":true}),makeQuery(id+"F3.opExtrude","SWEPT_FACE",FACE,{"disambiguationData":[OSD([sQuery(id+"F2.wireOp",EDGE,"E18.0")])]})]});
            var Q62;
            Q62=makeQuery(id+"F3.boolean.opBoolean","INTERSECT",EDGE,{"derivedFrom":[makeQuery(id+"F1.opExtrude","CAP_FACE",FACE,{"disambiguationData":[OSD([sQuery(id+"F0.wireOp",EDGE,"E4.0"),sQuery(id+"F0.wireOp",EDGE,"E4.1"),sQuery(id+"F0.wireOp",EDGE,"E4.2"),sQuery(id+"F0.wireOp",EDGE,"E4.3"),sQuery(id+"F0.wireOp",EDGE,"E4.4"),sQuery(id+"F0.wireOp",EDGE,"E4.5"),sQuery(id+"F0.wireOp",EDGE,"E5.0"),sQuery(id+"F0.wireOp",EDGE,"E5.1"),sQuery(id+"F0.wireOp",EDGE,"E5.2"),sQuery(id+"F0.wireOp",EDGE,"E5.3"),sQuery(id+"F0.wireOp",EDGE,"E5.4"),sQuery(id+"F0.wireOp",EDGE,"E5.5"),sQuery(id+"F0.wireOp",EDGE,"E6.0"),sQuery(id+"F0.wireOp",EDGE,"E6.1"),sQuery(id+"F0.wireOp",EDGE,"E6.2"),sQuery(id+"F0.wireOp",EDGE,"E6.3"),sQuery(id+"F0.wireOp",EDGE,"E6.4"),sQuery(id+"F0.wireOp",EDGE,"E6.5"),sQuery(id+"F0.wireOp",EDGE,"E7"),sQuery(id+"F0.wireOp",EDGE,"E8"),sQuery(id+"F0.wireOp",EDGE,"E9"),sQuery(id+"F0.wireOp",EDGE,"E10"),sQuery(id+"F0.wireOp",EDGE,"E12"),sQuery(id+"F0.wireOp",EDGE,"E13"),sQuery(id+"F0.wireOp",EDGE,"E14")])],"isStart":true}),makeQuery(id+"F3.opExtrude","SWEPT_FACE",FACE,{"disambiguationData":[OSD([sQuery(id+"F2.wireOp",EDGE,"E36")])]})]});
            var Q63;
            Q63=makeQuery(id+"F3.boolean.opBoolean","INTERSECT",EDGE,{"derivedFrom":[makeQuery(id+"F1.opExtrude","CAP_FACE",FACE,{"disambiguationData":[OSD([sQuery(id+"F0.wireOp",EDGE,"E4.0"),sQuery(id+"F0.wireOp",EDGE,"E4.1"),sQuery(id+"F0.wireOp",EDGE,"E4.2"),sQuery(id+"F0.wireOp",EDGE,"E4.3"),sQuery(id+"F0.wireOp",EDGE,"E4.4"),sQuery(id+"F0.wireOp",EDGE,"E4.5"),sQuery(id+"F0.wireOp",EDGE,"E5.0"),sQuery(id+"F0.wireOp",EDGE,"E5.1"),sQuery(id+"F0.wireOp",EDGE,"E5.2"),sQuery(id+"F0.wireOp",EDGE,"E5.3"),sQuery(id+"F0.wireOp",EDGE,"E5.4"),sQuery(id+"F0.wireOp",EDGE,"E5.5"),sQuery(id+"F0.wireOp",EDGE,"E6.0"),sQuery(id+"F0.wireOp",EDGE,"E6.1"),sQuery(id+"F0.wireOp",EDGE,"E6.2"),sQuery(id+"F0.wireOp",EDGE,"E6.3"),sQuery(id+"F0.wireOp",EDGE,"E6.4"),sQuery(id+"F0.wireOp",EDGE,"E6.5"),sQuery(id+"F0.wireOp",EDGE,"E7"),sQuery(id+"F0.wireOp",EDGE,"E8"),sQuery(id+"F0.wireOp",EDGE,"E9"),sQuery(id+"F0.wireOp",EDGE,"E10"),sQuery(id+"F0.wireOp",EDGE,"E12"),sQuery(id+"F0.wireOp",EDGE,"E13"),sQuery(id+"F0.wireOp",EDGE,"E14")])],"isStart":true}),makeQuery(id+"F3.opExtrude","SWEPT_FACE",FACE,{"disambiguationData":[OSD([sQuery(id+"F2.wireOp",EDGE,"E19.1")])]})]});
            var Q64;
            Q64=makeQuery(id+"F3.boolean.opBoolean","INTERSECT",EDGE,{"derivedFrom":[makeQuery(id+"F1.opExtrude","CAP_FACE",FACE,{"disambiguationData":[OSD([sQuery(id+"F0.wireOp",EDGE,"E4.0"),sQuery(id+"F0.wireOp",EDGE,"E4.1"),sQuery(id+"F0.wireOp",EDGE,"E4.2"),sQuery(id+"F0.wireOp",EDGE,"E4.3"),sQuery(id+"F0.wireOp",EDGE,"E4.4"),sQuery(id+"F0.wireOp",EDGE,"E4.5"),sQuery(id+"F0.wireOp",EDGE,"E5.0"),sQuery(id+"F0.wireOp",EDGE,"E5.1"),sQuery(id+"F0.wireOp",EDGE,"E5.2"),sQuery(id+"F0.wireOp",EDGE,"E5.3"),sQuery(id+"F0.wireOp",EDGE,"E5.4"),sQuery(id+"F0.wireOp",EDGE,"E5.5"),sQuery(id+"F0.wireOp",EDGE,"E6.0"),sQuery(id+"F0.wireOp",EDGE,"E6.1"),sQuery(id+"F0.wireOp",EDGE,"E6.2"),sQuery(id+"F0.wireOp",EDGE,"E6.3"),sQuery(id+"F0.wireOp",EDGE,"E6.4"),sQuery(id+"F0.wireOp",EDGE,"E6.5"),sQuery(id+"F0.wireOp",EDGE,"E7"),sQuery(id+"F0.wireOp",EDGE,"E8"),sQuery(id+"F0.wireOp",EDGE,"E9"),sQuery(id+"F0.wireOp",EDGE,"E10"),sQuery(id+"F0.wireOp",EDGE,"E12"),sQuery(id+"F0.wireOp",EDGE,"E13"),sQuery(id+"F0.wireOp",EDGE,"E14")])],"isStart":true}),makeQuery(id+"F3.opExtrude","SWEPT_FACE",FACE,{"disambiguationData":[OSD([sQuery(id+"F2.wireOp",EDGE,"E20.trimOffspring")])]})]});
            var Q65;
            Q65=makeQuery(id+"F3.boolean.opBoolean","INTERSECT",EDGE,{"derivedFrom":[makeQuery(id+"F1.opExtrude","CAP_FACE",FACE,{"disambiguationData":[OSD([sQuery(id+"F0.wireOp",EDGE,"E4.0"),sQuery(id+"F0.wireOp",EDGE,"E4.1"),sQuery(id+"F0.wireOp",EDGE,"E4.2"),sQuery(id+"F0.wireOp",EDGE,"E4.3"),sQuery(id+"F0.wireOp",EDGE,"E4.4"),sQuery(id+"F0.wireOp",EDGE,"E4.5"),sQuery(id+"F0.wireOp",EDGE,"E5.0"),sQuery(id+"F0.wireOp",EDGE,"E5.1"),sQuery(id+"F0.wireOp",EDGE,"E5.2"),sQuery(id+"F0.wireOp",EDGE,"E5.3"),sQuery(id+"F0.wireOp",EDGE,"E5.4"),sQuery(id+"F0.wireOp",EDGE,"E5.5"),sQuery(id+"F0.wireOp",EDGE,"E6.0"),sQuery(id+"F0.wireOp",EDGE,"E6.1"),sQuery(id+"F0.wireOp",EDGE,"E6.2"),sQuery(id+"F0.wireOp",EDGE,"E6.3"),sQuery(id+"F0.wireOp",EDGE,"E6.4"),sQuery(id+"F0.wireOp",EDGE,"E6.5"),sQuery(id+"F0.wireOp",EDGE,"E7"),sQuery(id+"F0.wireOp",EDGE,"E8"),sQuery(id+"F0.wireOp",EDGE,"E9"),sQuery(id+"F0.wireOp",EDGE,"E10"),sQuery(id+"F0.wireOp",EDGE,"E12"),sQuery(id+"F0.wireOp",EDGE,"E13"),sQuery(id+"F0.wireOp",EDGE,"E14")])],"isStart":true}),makeQuery(id+"F3.opExtrude","SWEPT_FACE",FACE,{"disambiguationData":[OSD([sQuery(id+"F2.wireOp",EDGE,"E18.1")])]})]});
            var Q66;
            Q66=makeQuery(id+"F3.boolean.opBoolean","INTERSECT",EDGE,{"derivedFrom":[makeQuery(id+"F1.opExtrude","CAP_FACE",FACE,{"disambiguationData":[OSD([sQuery(id+"F0.wireOp",EDGE,"E4.0"),sQuery(id+"F0.wireOp",EDGE,"E4.1"),sQuery(id+"F0.wireOp",EDGE,"E4.2"),sQuery(id+"F0.wireOp",EDGE,"E4.3"),sQuery(id+"F0.wireOp",EDGE,"E4.4"),sQuery(id+"F0.wireOp",EDGE,"E4.5"),sQuery(id+"F0.wireOp",EDGE,"E5.0"),sQuery(id+"F0.wireOp",EDGE,"E5.1"),sQuery(id+"F0.wireOp",EDGE,"E5.2"),sQuery(id+"F0.wireOp",EDGE,"E5.3"),sQuery(id+"F0.wireOp",EDGE,"E5.4"),sQuery(id+"F0.wireOp",EDGE,"E5.5"),sQuery(id+"F0.wireOp",EDGE,"E6.0"),sQuery(id+"F0.wireOp",EDGE,"E6.1"),sQuery(id+"F0.wireOp",EDGE,"E6.2"),sQuery(id+"F0.wireOp",EDGE,"E6.3"),sQuery(id+"F0.wireOp",EDGE,"E6.4"),sQuery(id+"F0.wireOp",EDGE,"E6.5"),sQuery(id+"F0.wireOp",EDGE,"E7"),sQuery(id+"F0.wireOp",EDGE,"E8"),sQuery(id+"F0.wireOp",EDGE,"E9"),sQuery(id+"F0.wireOp",EDGE,"E10"),sQuery(id+"F0.wireOp",EDGE,"E12"),sQuery(id+"F0.wireOp",EDGE,"E13"),sQuery(id+"F0.wireOp",EDGE,"E14")])],"isStart":true}),makeQuery(id+"F3.opExtrude","SWEPT_FACE",FACE,{"disambiguationData":[OSD([sQuery(id+"F2.wireOp",EDGE,"E17.1")])]})]});
            var Q67;
            Q67=makeQuery(id+"F3.boolean.opBoolean","INTERSECT",EDGE,{"derivedFrom":[makeQuery(id+"F1.opExtrude","CAP_FACE",FACE,{"disambiguationData":[OSD([sQuery(id+"F0.wireOp",EDGE,"E4.0"),sQuery(id+"F0.wireOp",EDGE,"E4.1"),sQuery(id+"F0.wireOp",EDGE,"E4.2"),sQuery(id+"F0.wireOp",EDGE,"E4.3"),sQuery(id+"F0.wireOp",EDGE,"E4.4"),sQuery(id+"F0.wireOp",EDGE,"E4.5"),sQuery(id+"F0.wireOp",EDGE,"E5.0"),sQuery(id+"F0.wireOp",EDGE,"E5.1"),sQuery(id+"F0.wireOp",EDGE,"E5.2"),sQuery(id+"F0.wireOp",EDGE,"E5.3"),sQuery(id+"F0.wireOp",EDGE,"E5.4"),sQuery(id+"F0.wireOp",EDGE,"E5.5"),sQuery(id+"F0.wireOp",EDGE,"E6.0"),sQuery(id+"F0.wireOp",EDGE,"E6.1"),sQuery(id+"F0.wireOp",EDGE,"E6.2"),sQuery(id+"F0.wireOp",EDGE,"E6.3"),sQuery(id+"F0.wireOp",EDGE,"E6.4"),sQuery(id+"F0.wireOp",EDGE,"E6.5"),sQuery(id+"F0.wireOp",EDGE,"E7"),sQuery(id+"F0.wireOp",EDGE,"E8"),sQuery(id+"F0.wireOp",EDGE,"E9"),sQuery(id+"F0.wireOp",EDGE,"E10"),sQuery(id+"F0.wireOp",EDGE,"E12"),sQuery(id+"F0.wireOp",EDGE,"E13"),sQuery(id+"F0.wireOp",EDGE,"E14")])],"isStart":true}),makeQuery(id+"F3.opExtrude","SWEPT_FACE",FACE,{"disambiguationData":[OSD([sQuery(id+"F2.wireOp",EDGE,"E17.0")])]})]});
            var Q68;
            Q68=makeQuery(id+"F3.boolean.opBoolean","INTERSECT",EDGE,{"derivedFrom":[makeQuery(id+"F1.opExtrude","CAP_FACE",FACE,{"disambiguationData":[OSD([sQuery(id+"F0.wireOp",EDGE,"E4.0"),sQuery(id+"F0.wireOp",EDGE,"E4.1"),sQuery(id+"F0.wireOp",EDGE,"E4.2"),sQuery(id+"F0.wireOp",EDGE,"E4.3"),sQuery(id+"F0.wireOp",EDGE,"E4.4"),sQuery(id+"F0.wireOp",EDGE,"E4.5"),sQuery(id+"F0.wireOp",EDGE,"E5.0"),sQuery(id+"F0.wireOp",EDGE,"E5.1"),sQuery(id+"F0.wireOp",EDGE,"E5.2"),sQuery(id+"F0.wireOp",EDGE,"E5.3"),sQuery(id+"F0.wireOp",EDGE,"E5.4"),sQuery(id+"F0.wireOp",EDGE,"E5.5"),sQuery(id+"F0.wireOp",EDGE,"E6.0"),sQuery(id+"F0.wireOp",EDGE,"E6.1"),sQuery(id+"F0.wireOp",EDGE,"E6.2"),sQuery(id+"F0.wireOp",EDGE,"E6.3"),sQuery(id+"F0.wireOp",EDGE,"E6.4"),sQuery(id+"F0.wireOp",EDGE,"E6.5"),sQuery(id+"F0.wireOp",EDGE,"E7"),sQuery(id+"F0.wireOp",EDGE,"E8"),sQuery(id+"F0.wireOp",EDGE,"E9"),sQuery(id+"F0.wireOp",EDGE,"E10"),sQuery(id+"F0.wireOp",EDGE,"E12"),sQuery(id+"F0.wireOp",EDGE,"E13"),sQuery(id+"F0.wireOp",EDGE,"E14")])],"isStart":true}),makeQuery(id+"F3.opExtrude","SWEPT_FACE",FACE,{"disambiguationData":[OSD([sQuery(id+"F2.wireOp",EDGE,"E15.0")])]})]});
            var Q69;
            Q69=makeQuery(id+"F3.boolean.opBoolean","INTERSECT",EDGE,{"derivedFrom":[makeQuery(id+"F1.opExtrude","CAP_FACE",FACE,{"disambiguationData":[OSD([sQuery(id+"F0.wireOp",EDGE,"E4.0"),sQuery(id+"F0.wireOp",EDGE,"E4.1"),sQuery(id+"F0.wireOp",EDGE,"E4.2"),sQuery(id+"F0.wireOp",EDGE,"E4.3"),sQuery(id+"F0.wireOp",EDGE,"E4.4"),sQuery(id+"F0.wireOp",EDGE,"E4.5"),sQuery(id+"F0.wireOp",EDGE,"E5.0"),sQuery(id+"F0.wireOp",EDGE,"E5.1"),sQuery(id+"F0.wireOp",EDGE,"E5.2"),sQuery(id+"F0.wireOp",EDGE,"E5.3"),sQuery(id+"F0.wireOp",EDGE,"E5.4"),sQuery(id+"F0.wireOp",EDGE,"E5.5"),sQuery(id+"F0.wireOp",EDGE,"E6.0"),sQuery(id+"F0.wireOp",EDGE,"E6.1"),sQuery(id+"F0.wireOp",EDGE,"E6.2"),sQuery(id+"F0.wireOp",EDGE,"E6.3"),sQuery(id+"F0.wireOp",EDGE,"E6.4"),sQuery(id+"F0.wireOp",EDGE,"E6.5"),sQuery(id+"F0.wireOp",EDGE,"E7"),sQuery(id+"F0.wireOp",EDGE,"E8"),sQuery(id+"F0.wireOp",EDGE,"E9"),sQuery(id+"F0.wireOp",EDGE,"E10"),sQuery(id+"F0.wireOp",EDGE,"E12"),sQuery(id+"F0.wireOp",EDGE,"E13"),sQuery(id+"F0.wireOp",EDGE,"E14")])],"isStart":true}),makeQuery(id+"F3.opExtrude","SWEPT_FACE",FACE,{"disambiguationData":[OSD([sQuery(id+"F2.wireOp",EDGE,"E15.1")])]})]});
            fillet(context, id + "F5", {"entities" : qUnion([Q0, Q1, Q2, Q3, Q4, Q5, Q6, Q7, Q8, Q9, Q10, Q11, Q12, Q13, Q14, Q15, Q16, Q17, Q18, Q19, Q20, Q21, Q22, Q23, Q24, Q25, Q26, Q27, Q28, Q29, Q30, Q31, Q32, Q33, Q34, Q35, Q36, Q37, Q38, Q39, Q40, Q41, Q42, Q43, Q44, Q45, Q46, Q47, Q48, Q49, Q50, Q51, Q52, Q53, Q54, Q55, Q56, Q57, Q58, Q59, Q60, Q61, Q62, Q63, Q64, Q65, Q66, Q67, Q68, Q69]), "radius" : 1 * mm, "tangentPropagation" : true, "allowEdgeOverflow" : false});
        }
    });
